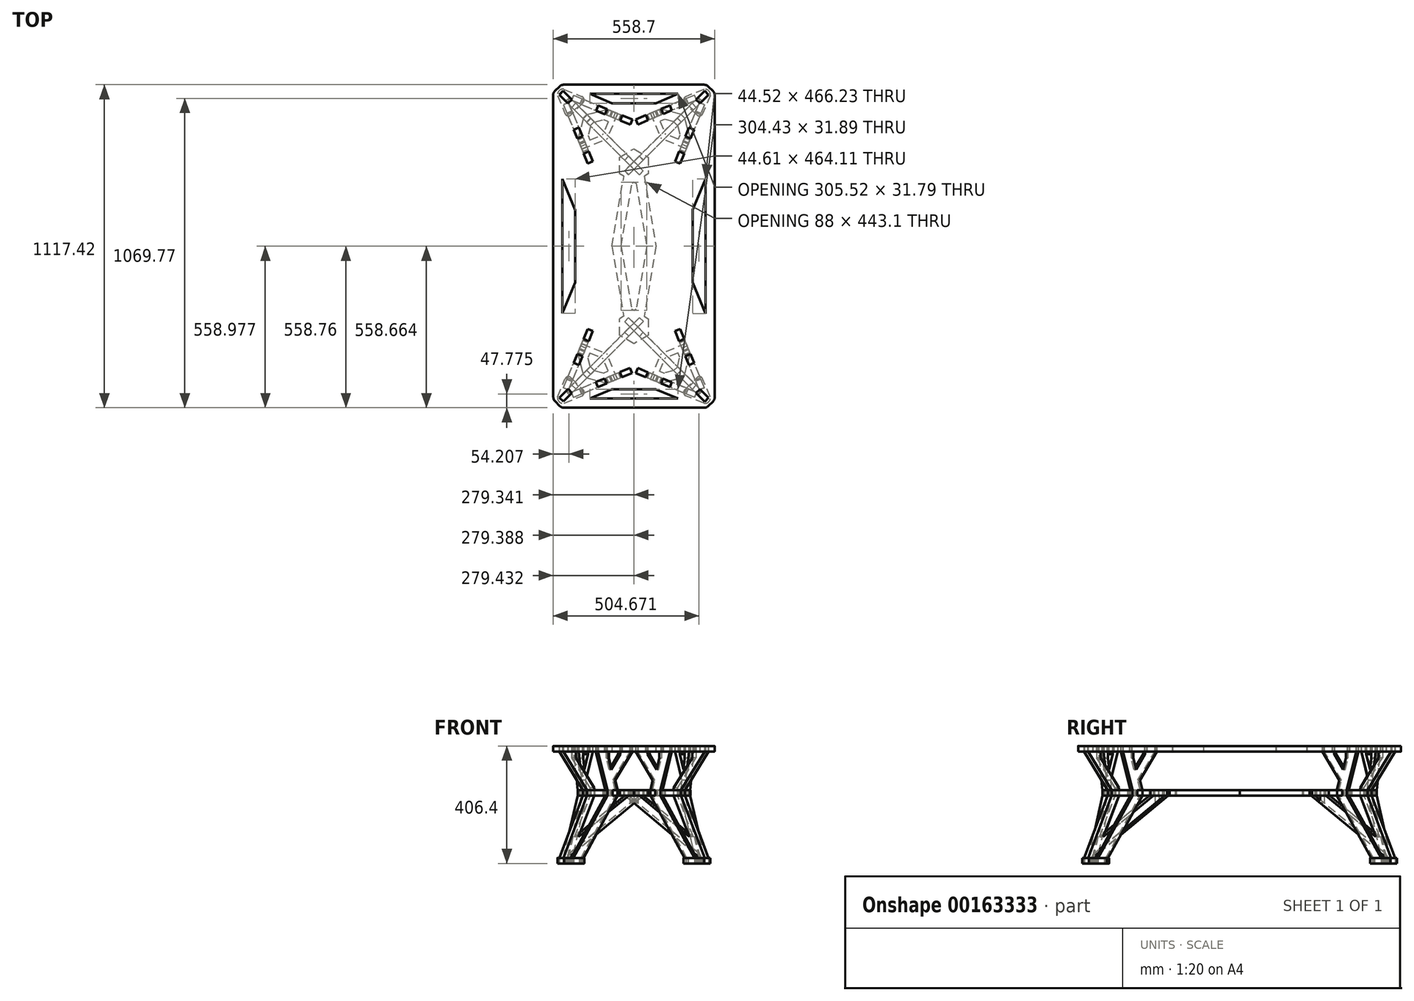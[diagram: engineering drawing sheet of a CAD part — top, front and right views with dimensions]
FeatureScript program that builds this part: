
annotation { "Feature Type Name" : "Feature", "Feature Type Description" : "" }
export const myFeature = defineFeature(function(context is Context, id is Id, definition is map)
    precondition{}
    {
        {
            var Q0;
            Q0=qCreatedBy(makeId("Top.planeOp"),FACE);
            var sketch = newSketch(context, id + "F0", { "sketchPlane" : qUnion([Q0])});
            skLineSegment(sketch, "E0.bottom", {"start": v(0.12, 1117.48) * mm, "end": v(558.92, 1117.48) * mm});
            skLineSegment(sketch, "E0.top", {"start": v(0.12, -0.12) * mm, "end": v(558.92, -0.12) * mm});
            skLineSegment(sketch, "E0.left", {"start": v(0.12, 1117.48) * mm, "end": v(0.12, -0.12) * mm});
            skLineSegment(sketch, "E0.right", {"start": v(558.92, 1117.48) * mm, "end": v(558.92, -0.12) * mm});
            skLineSegment(sketch, "E1", {"start": v(0.12, -0.12) * mm, "end": v(425.24, 425) * mm, "construction": true});
            skLineSegment(sketch, "E2", {"start": v(558.92, 1117.48) * mm, "end": v(139.82, 698.5) * mm, "construction": true});
            skLineSegment(sketch, "E3", {"start": v(0.12, 1117.48) * mm, "end": v(139.82, 1117.48) * mm});
            skLineSegment(sketch, "E4", {"start": v(139.82, 1117.48) * mm, "end": v(139.82, -0.12) * mm, "construction": true});
            skLineSegment(sketch, "E5", {"start": v(558.92, -0.12) * mm, "end": v(419.22, -0.12) * mm});
            skPoint(sketch, "E6", {"position": v(419.22, 1117.48) * mm});
            skLineSegment(sketch, "E7", {"start": v(419.22, 1117.48) * mm, "end": v(427.8, -0.12) * mm, "construction": true});
            skLineSegment(sketch, "E8.MirrorCS", {"start": v(422.46, 695.18) * mm, "end": v(0.12, 1117.48) * mm, "construction": true});
            skPoint(sketch, "E9", {"position": v(117.33, 48.6) * mm});
            skPoint(sketch, "E10", {"position": v(48.57, 117.26) * mm});
            skLineSegment(sketch, "E11", {"start": v(60.73, 105.12) * mm, "end": v(105.17, 60.75) * mm});
            skLineSegment(sketch, "E12.0", {"start": v(5.87, -2.43) * mm, "end": v(54.47, 114.9) * mm, "construction": true});
            skLineSegment(sketch, "E13.0", {"start": v(-2.43, 5.87) * mm, "end": v(114.9, 54.47) * mm, "construction": true});
            skLineSegment(sketch, "E14", {"start": v(21.87, 35.21) * mm, "end": v(44.32, 57.67) * mm});
            skLineSegment(sketch, "E15", {"start": v(35.34, 21.74) * mm, "end": v(57.8, 44.2) * mm});
            skLineSegment(sketch, "E16", {"start": v(44.32, 57.67) * mm, "end": v(57.8, 44.2) * mm});
            skLineSegment(sketch, "E17", {"start": v(21.87, 35.21) * mm, "end": v(35.34, 21.74) * mm});
            skLineSegment(sketch, "E18.0", {"start": v(44.06, 112.79) * mm, "end": v(112.85, 44.1) * mm, "construction": true});
            skLineSegment(sketch, "E19", {"start": v(47.74, 98.66) * mm, "end": v(65.34, 91.37) * mm});
            skLineSegment(sketch, "E20", {"start": v(65.34, 91.37) * mm, "end": v(53.2, 62.04) * mm});
            skLineSegment(sketch, "E21", {"start": v(53.2, 62.04) * mm, "end": v(35.6, 69.33) * mm});
            skLineSegment(sketch, "E22", {"start": v(35.6, 69.33) * mm, "end": v(47.74, 98.66) * mm});
            skLineSegment(sketch, "E23", {"start": v(98.94, 47.85) * mm, "end": v(91.65, 65.45) * mm});
            skLineSegment(sketch, "E24", {"start": v(91.65, 65.45) * mm, "end": v(62.3, 53.3) * mm});
            skLineSegment(sketch, "E25", {"start": v(62.3, 53.3) * mm, "end": v(69.6, 35.7) * mm});
            skLineSegment(sketch, "E26", {"start": v(69.6, 35.7) * mm, "end": v(98.94, 47.85) * mm});
            skPoint(sketch, "E27", {"position": v(65.95, 44.5) * mm});
            skLineSegment(sketch, "E28", {"start": v(95.3, 56.65) * mm, "end": v(426.3, 193.77) * mm, "construction": true});
            skPoint(sketch, "E29", {"position": v(44.4, 65.69) * mm});
            skLineSegment(sketch, "E30", {"start": v(44.4, 65.69) * mm, "end": v(139.82, 296.06) * mm, "construction": true});
            skPoint(sketch, "E31.orphan", {"position": v(56.54, 95.02) * mm});
            skLineSegment(sketch, "E32", {"start": v(558.92, -0.12) * mm, "end": v(530.98, 27.81) * mm, "construction": true});
            skLineSegment(sketch, "E33", {"start": v(558.92, -0.12) * mm, "end": v(555.48, 8.18) * mm});
            skLineSegment(sketch, "E34", {"start": v(558.92, -0.12) * mm, "end": v(550.62, 3.32) * mm});
            skLineSegment(sketch, "E35", {"start": v(441.55, 48.52) * mm, "end": v(446.41, 53.37) * mm});
            skLineSegment(sketch, "E36.0", {"start": v(446.04, 44.02) * mm, "end": v(514.81, 112.71) * mm, "construction": true});
            skLineSegment(sketch, "E37.0", {"start": v(553.05, -2.56) * mm, "end": v(504.46, 114.77) * mm, "construction": true});
            skLineSegment(sketch, "E38.0", {"start": v(561.3, 5.76) * mm, "end": v(443.98, 54.38) * mm, "construction": true});
            skLineSegment(sketch, "E39", {"start": v(524.24, 21.07) * mm, "end": v(501.79, 43.52) * mm});
            skLineSegment(sketch, "E40", {"start": v(501.79, 43.52) * mm, "end": v(515.26, 57) * mm});
            skLineSegment(sketch, "E41", {"start": v(515.26, 57) * mm, "end": v(537.7, 34.54) * mm});
            skLineSegment(sketch, "E42", {"start": v(524.24, 21.07) * mm, "end": v(537.7, 34.54) * mm});
            skLineSegment(sketch, "E43", {"start": v(460.07, 47.71) * mm, "end": v(467.3, 65.18) * mm});
            skLineSegment(sketch, "E44", {"start": v(467.3, 65.18) * mm, "end": v(496.64, 53.02) * mm});
            skLineSegment(sketch, "E45", {"start": v(496.64, 53.02) * mm, "end": v(489.4, 35.56) * mm});
            skLineSegment(sketch, "E46", {"start": v(489.4, 35.56) * mm, "end": v(460.07, 47.71) * mm});
            skLineSegment(sketch, "E47", {"start": v(511.05, 98.85) * mm, "end": v(493.45, 91.56) * mm});
            skLineSegment(sketch, "E48", {"start": v(493.45, 91.56) * mm, "end": v(505.6, 62.23) * mm});
            skLineSegment(sketch, "E49", {"start": v(505.6, 62.23) * mm, "end": v(523.2, 69.52) * mm});
            skLineSegment(sketch, "E50", {"start": v(523.2, 69.52) * mm, "end": v(511.05, 98.85) * mm});
            skPoint(sketch, "E51", {"position": v(493.02, 44.29) * mm});
            skPoint(sketch, "E52", {"position": v(514.4, 65.87) * mm});
            skLineSegment(sketch, "E53", {"start": v(514.4, 65.87) * mm, "end": v(425.64, 280.16) * mm, "construction": true});
            skLineSegment(sketch, "E54", {"start": v(493.02, 44.29) * mm, "end": v(139.82, 190.66) * mm, "construction": true});
            skPoint(sketch, "E55.first.point", {"position": v(7.35, 17.5) * mm});
            skPoint(sketch, "E55.second.point", {"position": v(17.7, 7.2) * mm});
            skArc(sketch, "E56", {"start": v(7.35, 17.5) * mm, "mid": v(9.84, 9.66) * mm, "end": v(17.7, 7.2) * mm, "construction": true});
            skPoint(sketch, "E57", {"position": v(103.85, 62.06) * mm});
            skPoint(sketch, "E58", {"position": v(99.73, 41.31) * mm});
            skArc(sketch, "E59", {"start": v(99.73, 41.31) * mm, "mid": v(107.37, 50.58) * mm, "end": v(103.85, 62.06) * mm});
            skPoint(sketch, "E60", {"position": v(41.28, 99.66) * mm});
            skPoint(sketch, "E61", {"position": v(62.05, 103.8) * mm});
            skArc(sketch, "E62", {"start": v(62.05, 103.8) * mm, "mid": v(50.55, 107.31) * mm, "end": v(41.28, 99.66) * mm});
            skLineSegment(sketch, "E63.trimOffspring", {"start": v(15.71, 37.76) * mm, "end": v(41.33, 99.8) * mm});
            skLineSegment(sketch, "E64.trimOffspring", {"start": v(37.9, 15.6) * mm, "end": v(99.85, 41.36) * mm});
            skLineSegment(sketch, "E65", {"start": v(35.34, 21.74) * mm, "end": v(37.9, 15.6) * mm, "construction": true});
            skLineSegment(sketch, "E66", {"start": v(21.87, 35.21) * mm, "end": v(15.71, 37.76) * mm, "construction": true});
            skArc(sketch, "E67", {"start": v(15.71, 37.76) * mm, "mid": v(21, 20.86) * mm, "end": v(37.9, 15.6) * mm});
            skPoint(sketch, "E68", {"position": v(459.15, 41.22) * mm});
            skPoint(sketch, "E69", {"position": v(517.74, 99.3) * mm});
            skPoint(sketch, "E70", {"position": v(455.03, 61.98) * mm});
            skPoint(sketch, "E71", {"position": v(496.84, 103.74) * mm});
            skLineSegment(sketch, "E72", {"start": v(524.24, 21.07) * mm, "end": v(521.82, 15.25) * mm, "construction": true});
            skLineSegment(sketch, "E73", {"start": v(537.7, 34.54) * mm, "end": v(543.56, 36.96) * mm, "construction": true});
            skArc(sketch, "E74", {"start": v(455.03, 61.98) * mm, "mid": v(451.52, 50.5) * mm, "end": v(459.15, 41.22) * mm});
            skArc(sketch, "E75", {"start": v(517.74, 99.3) * mm, "mid": v(508.5, 107.22) * mm, "end": v(496.84, 103.74) * mm});
            skArc(sketch, "E76", {"start": v(521.82, 15.25) * mm, "mid": v(538.2, 20.6) * mm, "end": v(543.56, 36.96) * mm});
            skLineSegment(sketch, "E77.trimOffspring", {"start": v(521.82, 15.25) * mm, "end": v(459.08, 41.25) * mm});
            skLineSegment(sketch, "E78.trimOffspring", {"start": v(543.56, 36.96) * mm, "end": v(517.44, 100.01) * mm});
            skLineSegment(sketch, "E79.trimOffspring", {"start": v(512.95, 110.85) * mm, "end": v(510.32, 117.2) * mm});
            skLineSegment(sketch, "E80.trimOffspring", {"start": v(505.46, 112.35) * mm, "end": v(510.32, 117.2) * mm});
            skLineSegment(sketch, "E81.trimOffspring", {"start": v(453.65, 60.6) * mm, "end": v(498.17, 105.06) * mm});
            skLineSegment(sketch, "E82.trimOffspring", {"start": v(447.9, 45.88) * mm, "end": v(441.55, 48.52) * mm});
            skLineSegment(sketch, "E83", {"start": v(37.26, 1102.12) * mm, "end": v(99.78, 1076.27) * mm});
            skLineSegment(sketch, "E84", {"start": v(15.48, 1080.34) * mm, "end": v(41.33, 1017.86) * mm});
            skLineSegment(sketch, "E85", {"start": v(103.9, 1055.58) * mm, "end": v(62.08, 1013.73) * mm});
            skLineSegment(sketch, "E86.0", {"start": v(11.84, 1105.76) * mm, "end": v(106.12, 1066.78) * mm, "construction": true});
            skLineSegment(sketch, "E86.1", {"start": v(11.84, 1105.76) * mm, "end": v(50.84, 1011.47) * mm, "construction": true});
            skLineSegment(sketch, "E86.2", {"start": v(106.12, 1066.78) * mm, "end": v(50.84, 1011.47) * mm, "construction": true});
            skLineSegment(sketch, "E87", {"start": v(21.37, 1082.78) * mm, "end": v(43.83, 1060.33) * mm});
            skLineSegment(sketch, "E88", {"start": v(34.84, 1096.25) * mm, "end": v(57.29, 1073.8) * mm});
            skLineSegment(sketch, "E89", {"start": v(43.83, 1060.33) * mm, "end": v(57.29, 1073.8) * mm});
            skLineSegment(sketch, "E90", {"start": v(21.37, 1082.78) * mm, "end": v(34.84, 1096.25) * mm});
            skLineSegment(sketch, "E91", {"start": v(47.82, 1018.79) * mm, "end": v(65.42, 1026.07) * mm});
            skLineSegment(sketch, "E92", {"start": v(65.42, 1026.07) * mm, "end": v(53.28, 1055.4) * mm});
            skLineSegment(sketch, "E93", {"start": v(53.28, 1055.4) * mm, "end": v(35.68, 1048.13) * mm});
            skLineSegment(sketch, "E94", {"start": v(35.68, 1048.13) * mm, "end": v(47.82, 1018.79) * mm});
            skLineSegment(sketch, "E95", {"start": v(100.12, 1069.26) * mm, "end": v(92.84, 1051.65) * mm});
            skLineSegment(sketch, "E96", {"start": v(92.84, 1051.65) * mm, "end": v(63.5, 1063.78) * mm});
            skLineSegment(sketch, "E97", {"start": v(63.5, 1063.78) * mm, "end": v(70.78, 1081.39) * mm});
            skLineSegment(sketch, "E98", {"start": v(70.78, 1081.39) * mm, "end": v(100.12, 1069.26) * mm});
            skPoint(sketch, "E99", {"position": v(99.73, 1076.3) * mm});
            skPoint(sketch, "E100", {"position": v(103.87, 1055.54) * mm});
            skPoint(sketch, "E101", {"position": v(62.08, 1013.73) * mm});
            skPoint(sketch, "E102", {"position": v(41.33, 1017.86) * mm});
            skLineSegment(sketch, "E103", {"start": v(34.84, 1096.25) * mm, "end": v(37.26, 1102.12) * mm, "construction": true});
            skLineSegment(sketch, "E104", {"start": v(21.37, 1082.78) * mm, "end": v(15.48, 1080.34) * mm, "construction": true});
            skArc(sketch, "E105", {"start": v(37.26, 1102.12) * mm, "mid": v(20.83, 1096.78) * mm, "end": v(15.48, 1080.34) * mm});
            skArc(sketch, "E106", {"start": v(41.33, 1017.86) * mm, "mid": v(50.6, 1010.25) * mm, "end": v(62.08, 1013.73) * mm});
            skArc(sketch, "E107", {"start": v(103.87, 1055.54) * mm, "mid": v(107.36, 1067.02) * mm, "end": v(99.73, 1076.3) * mm});
            skPoint(sketch, "E108.orphan", {"position": v(117.33, 1069.01) * mm});
            skPoint(sketch, "E109.orphan", {"position": v(48.61, 1000.26) * mm});
            skPoint(sketch, "E110", {"position": v(67.14, 1072.59) * mm});
            skPoint(sketch, "E111", {"position": v(44.48, 1051.77) * mm});
            skLineSegment(sketch, "E112", {"start": v(67.14, 1072.59) * mm, "end": v(420.68, 926.4) * mm, "construction": true});
            skLineSegment(sketch, "E113", {"start": v(44.48, 1051.77) * mm, "end": v(139.82, 821.33) * mm, "construction": true});
            skLineSegment(sketch, "E114", {"start": v(543.54, 1080.37) * mm, "end": v(517.57, 1017.7) * mm});
            skLineSegment(sketch, "E115", {"start": v(521.77, 1102.1) * mm, "end": v(459, 1076.1) * mm});
            skLineSegment(sketch, "E116", {"start": v(496.86, 1013.59) * mm, "end": v(454.91, 1055.55) * mm});
            skLineSegment(sketch, "E117.0", {"start": v(547.18, 1105.75) * mm, "end": v(508.07, 1011.36) * mm, "construction": true});
            skLineSegment(sketch, "E117.1", {"start": v(547.18, 1105.75) * mm, "end": v(452.79, 1066.66) * mm, "construction": true});
            skLineSegment(sketch, "E117.2", {"start": v(508.07, 1011.36) * mm, "end": v(452.79, 1066.66) * mm, "construction": true});
            skLineSegment(sketch, "E118", {"start": v(524.18, 1096.28) * mm, "end": v(501.73, 1073.84) * mm});
            skLineSegment(sketch, "E119", {"start": v(501.73, 1073.84) * mm, "end": v(515.2, 1060.36) * mm});
            skLineSegment(sketch, "E120", {"start": v(515.2, 1060.36) * mm, "end": v(537.65, 1082.81) * mm});
            skLineSegment(sketch, "E121", {"start": v(537.65, 1082.81) * mm, "end": v(524.18, 1096.28) * mm});
            skLineSegment(sketch, "E122", {"start": v(511.1, 1018.66) * mm, "end": v(493.5, 1025.96) * mm});
            skLineSegment(sketch, "E123", {"start": v(493.5, 1025.96) * mm, "end": v(505.65, 1055.29) * mm});
            skLineSegment(sketch, "E124", {"start": v(505.65, 1055.29) * mm, "end": v(523.25, 1048) * mm});
            skLineSegment(sketch, "E125", {"start": v(523.25, 1048) * mm, "end": v(511.1, 1018.66) * mm});
            skLineSegment(sketch, "E126", {"start": v(460.07, 1069.68) * mm, "end": v(467.36, 1052.07) * mm});
            skLineSegment(sketch, "E127", {"start": v(467.36, 1052.07) * mm, "end": v(496.7, 1064.22) * mm});
            skLineSegment(sketch, "E128", {"start": v(496.7, 1064.22) * mm, "end": v(489.4, 1081.82) * mm});
            skLineSegment(sketch, "E129", {"start": v(489.4, 1081.82) * mm, "end": v(460.07, 1069.68) * mm});
            skPoint(sketch, "E130", {"position": v(517.6, 1017.75) * mm});
            skPoint(sketch, "E131", {"position": v(496.83, 1013.62) * mm});
            skPoint(sketch, "E132", {"position": v(455.05, 1055.42) * mm});
            skPoint(sketch, "E133", {"position": v(459.18, 1076.18) * mm});
            skLineSegment(sketch, "E134", {"start": v(524.18, 1096.28) * mm, "end": v(521.77, 1102.1) * mm, "construction": true});
            skLineSegment(sketch, "E135", {"start": v(537.65, 1082.81) * mm, "end": v(543.54, 1080.37) * mm, "construction": true});
            skArc(sketch, "E136", {"start": v(543.54, 1080.37) * mm, "mid": v(538.16, 1096.75) * mm, "end": v(521.77, 1102.1) * mm});
            skArc(sketch, "E137", {"start": v(459.18, 1076.18) * mm, "mid": v(451.52, 1066.91) * mm, "end": v(455.05, 1055.42) * mm});
            skArc(sketch, "E138", {"start": v(496.83, 1013.62) * mm, "mid": v(508.32, 1010.13) * mm, "end": v(517.6, 1017.75) * mm});
            skPoint(sketch, "E139.orphan", {"position": v(510.3, 1000.15) * mm});
            skPoint(sketch, "E140.orphan", {"position": v(441.58, 1068.89) * mm});
            skPoint(sketch, "E141", {"position": v(514.45, 1051.64) * mm});
            skPoint(sketch, "E142", {"position": v(493.05, 1073.02) * mm});
            skLineSegment(sketch, "E143", {"start": v(514.45, 1051.64) * mm, "end": v(421.45, 827.2) * mm, "construction": true});
            skLineSegment(sketch, "E144", {"start": v(493.05, 1073.02) * mm, "end": v(139.82, 926.75) * mm, "construction": true});
            skLineSegment(sketch, "E145.trimOffspring", {"start": v(508.53, 50.26) * mm, "end": v(139.82, 418.98) * mm, "construction": true});
            skSolve(sketch);
        }
        {
            var Q0;
            Q0=sQuery(id+"F0.wireOp",EDGE,"E1");
            var Q1;
            {var subQ1=sQuery(id+"F0.wireOp",EDGE,"E1");var subQ7=sQuery(id+"F0.wireOp",EDGE,"E4");var subQ9=makeQuery(id+"F0.imprint","INTERSECT",VERTEX,{"derivedFrom":[subQ1,subQ7]});Q1=makeQuery(id+"F0.imprint","IMPRINT",FACE,{"disambiguationData":[TD([[makeQuery(id+"F0.imprint","IMPRINT",EDGE,{"disambiguationData":[TD([[subQ9,-1.0]])],"derivedFrom":subQ1}),-1.0]])]});}
            cPlane(context, id + "F1", {"entities" : qUnion([Q0, Q1]), "cplaneType" : CPlaneType.LINE_ANGLE, "offset" : 25.4 * mm, "angle" : 90 * degree, "width" : 152.4 * mm, "height" : 152.4 * mm});
        }
        {
            var Q0;
            Q0=qCreatedBy(id+"F1.planeOp",FACE);
            var sketch = newSketch(context, id + "F2", { "sketchPlane" : qUnion([Q0])});
            skLineSegment(sketch, "E146", {"start": v(603.86, 0) * mm, "end": v(603.86, 406.4) * mm, "construction": true});
            skLineSegment(sketch, "E147.MirrorCS", {"start": v(72.14, 19.05) * mm, "end": v(76.5, 19.05) * mm});
            skLineSegment(sketch, "E148.MirrorCS", {"start": v(40.4, 387.35) * mm, "end": v(40.4, 406.4) * mm});
            skLineSegment(sketch, "E149.MirrorCS", {"start": v(40.4, 19.05) * mm, "end": v(40.4, 0) * mm});
            skLineSegment(sketch, "E150.MirrorCS", {"start": v(82.38, 406.4) * mm, "end": v(40.4, 406.4) * mm});
            skLineSegment(sketch, "E151.MirrorCS", {"start": v(40.4, 387.35) * mm, "end": v(603.86, 387.35) * mm, "construction": true});
            skLineSegment(sketch, "E152.MirrorCS", {"start": v(40.4, 406.4) * mm, "end": v(603.86, 406.4) * mm, "construction": true});
            skLineSegment(sketch, "E153.MirrorCS", {"start": v(40.4, 0) * mm, "end": v(40.4, 406.4) * mm, "construction": true});
            skPoint(sketch, "E154.MirrorP", {"position": v(40.4, 254) * mm});
            skLineSegment(sketch, "E155.MirrorCS", {"start": v(82.38, 387.35) * mm, "end": v(82.38, 406.4) * mm});
            skLineSegment(sketch, "E156.MirrorCS", {"start": v(40.4, 0) * mm, "end": v(72.14, 0) * mm});
            skLineSegment(sketch, "E157.MirrorCS", {"start": v(155.77, 254) * mm, "end": v(40.4, 387.35) * mm});
            skLineSegment(sketch, "E158.MirrorCS", {"start": v(72.14, 19.05) * mm, "end": v(72.14, 0) * mm});
            skLineSegment(sketch, "E159.MirrorCS", {"start": v(40.4, 19.05) * mm, "end": v(155.77, 234.95) * mm});
            skLineSegment(sketch, "E160.MirrorCS", {"start": v(76.5, 19.05) * mm, "end": v(603.86, 19.05) * mm, "construction": true});
            skLineSegment(sketch, "E161.MirrorCS", {"start": v(72.14, 0) * mm, "end": v(603.86, 0) * mm, "construction": true});
            skLineSegment(sketch, "E162.trimOffspring", {"start": v(115.25, 91.77) * mm, "end": v(191.77, 234.95) * mm});
            skLineSegment(sketch, "E163", {"start": v(82.67, 30.78) * mm, "end": v(76.5, 19.05) * mm});
            skLineSegment(sketch, "E164", {"start": v(40.4, 254) * mm, "end": v(155.77, 254) * mm, "construction": true});
            skLineSegment(sketch, "E165.0", {"start": v(40.4, 234.95) * mm, "end": v(191.77, 234.95) * mm, "construction": true});
            skLineSegment(sketch, "E166", {"start": v(82.67, 30.78) * mm, "end": v(431.82, 234.95) * mm});
            skLineSegment(sketch, "E167", {"start": v(191.77, 234.95) * mm, "end": v(191.77, 260.91) * mm});
            skLineSegment(sketch, "E168.trimOffspring", {"start": v(191.77, 260.91) * mm, "end": v(101.43, 365.33) * mm});
            skLineSegment(sketch, "E169.trimOffspring", {"start": v(173.77, 254) * mm, "end": v(360.6, 254) * mm, "construction": true});
            skLineSegment(sketch, "E170.trimOffspring", {"start": v(191.77, 234.95) * mm, "end": v(603.86, 234.95) * mm, "construction": true});
            skLineSegment(sketch, "E171", {"start": v(155.77, 254) * mm, "end": v(173.77, 254) * mm});
            skLineSegment(sketch, "E172", {"start": v(173.77, 254) * mm, "end": v(173.77, 234.95) * mm});
            skLineSegment(sketch, "E173", {"start": v(173.77, 234.95) * mm, "end": v(155.77, 234.95) * mm});
            skLineSegment(sketch, "E174", {"start": v(395.13, 0) * mm, "end": v(395.13, 406.4) * mm, "construction": true});
            skLineSegment(sketch, "E175", {"start": v(431.82, 234.95) * mm, "end": v(431.82, 254) * mm});
            skLineSegment(sketch, "E176", {"start": v(385.6, 207.92) * mm, "end": v(385.6, 254) * mm, "construction": true});
            skLineSegment(sketch, "E177", {"start": v(404.65, 219.06) * mm, "end": v(404.65, 254) * mm, "construction": true});
            skLineSegment(sketch, "E178.trimOffspring", {"start": v(431.82, 254) * mm, "end": v(603.86, 254) * mm, "construction": true});
            skLineSegment(sketch, "E179", {"start": v(360.12, 254) * mm, "end": v(385.6, 254) * mm});
            skLineSegment(sketch, "E180.0", {"start": v(115.25, 91.77) * mm, "end": v(360.12, 234.95) * mm});
            skLineSegment(sketch, "E181", {"start": v(360.12, 234.95) * mm, "end": v(360.12, 254) * mm});
            skLineSegment(sketch, "E182", {"start": v(404.65, 254) * mm, "end": v(404.65, 234.95) * mm});
            skLineSegment(sketch, "E183", {"start": v(404.65, 234.95) * mm, "end": v(385.6, 234.95) * mm});
            skLineSegment(sketch, "E184", {"start": v(385.6, 234.95) * mm, "end": v(385.6, 254) * mm});
            skLineSegment(sketch, "E185.trimOffspring", {"start": v(404.65, 254) * mm, "end": v(431.82, 254) * mm});
            skLineSegment(sketch, "E186", {"start": v(82.38, 387.35) * mm, "end": v(101.43, 387.35) * mm});
            skLineSegment(sketch, "E187", {"start": v(101.43, 365.33) * mm, "end": v(101.43, 387.35) * mm});
            skSolve(sketch);
        }
        {
            var Q0;
            Q0=makeQuery(id+"F2.imprint","IMPRINT",FACE,{"disambiguationData":[TD([[makeQuery(id+"F2.imprint","IMPRINT",EDGE,{"derivedFrom":sQuery(id+"F2.wireOp",EDGE,"E147.MirrorCS")}),1.0]])]});
            extrude(context, id + "F3", {"entities" : qUnion([Q0]), "endBound" : BoundingType.SYMMETRIC, "depth" : 19.05 * mm});
        }
        {
            var Q0;
            Q0=sQuery(id+"F0.wireOp",EDGE,"E28");
            cPlane(context, id + "F4", {"entities" : qUnion([Q0]), "cplaneType" : CPlaneType.LINE_ANGLE, "offset" : 25.4 * mm, "angle" : 0 * degree, "width" : 152.4 * mm, "height" : 152.4 * mm});
        }
        {
            var Q0;
            Q0=qCreatedBy(id+"F4.planeOp",FACE);
            var sketch = newSketch(context, id + "F5", { "sketchPlane" : qUnion([Q0])});
            skLineSegment(sketch, "E188", {"start": v(-442.84, 0) * mm, "end": v(-442.84, 406.4) * mm, "construction": true});
            skLineSegment(sketch, "E189.MirrorCS", {"start": v(-109.72, 19.05) * mm, "end": v(-114.91, 19.05) * mm});
            skLineSegment(sketch, "E190.MirrorCS", {"start": v(-77.97, 19.05) * mm, "end": v(-77.97, 0) * mm});
            skLineSegment(sketch, "E191.MirrorCS", {"start": v(-109.72, 0) * mm, "end": v(-109.72, 19.05) * mm});
            skLineSegment(sketch, "E192.MirrorCS", {"start": v(-77.97, 0) * mm, "end": v(-109.72, 0) * mm});
            skLineSegment(sketch, "E193.MirrorCS", {"start": v(-77.97, 234.95) * mm, "end": v(-206.36, 234.95) * mm, "construction": true});
            skLineSegment(sketch, "E194.MirrorCS", {"start": v(-77.97, 387.35) * mm, "end": v(-442.84, 387.35) * mm, "construction": true});
            skLineSegment(sketch, "E195.MirrorCS", {"start": v(-77.97, 0) * mm, "end": v(-442.84, 0) * mm, "construction": true});
            skLineSegment(sketch, "E196.MirrorCS", {"start": v(-77.97, 406.4) * mm, "end": v(-442.84, 406.4) * mm, "construction": true});
            skLineSegment(sketch, "E197.MirrorCS", {"start": v(-77.97, 0) * mm, "end": v(-77.97, 406.4) * mm, "construction": true});
            skLineSegment(sketch, "E198.MirrorCS", {"start": v(-309, 0) * mm, "end": v(-309, 406.4) * mm, "construction": true});
            skLineSegment(sketch, "E199", {"start": v(-77.97, 19.05) * mm, "end": v(-206.36, 234.95) * mm});
            skLineSegment(sketch, "E200", {"start": v(-206.36, 234.95) * mm, "end": v(-206.36, 254) * mm});
            skLineSegment(sketch, "E201", {"start": v(-206.36, 254) * mm, "end": v(-170.87, 387.35) * mm});
            skLineSegment(sketch, "E202", {"start": v(-170.87, 387.35) * mm, "end": v(-170.87, 406.4) * mm});
            skLineSegment(sketch, "E203", {"start": v(-220.38, 324.76) * mm, "end": v(-254.06, 377.42) * mm});
            skLineSegment(sketch, "E204.0", {"start": v(-234.34, 287.65) * mm, "end": v(-298.1, 387.35) * mm});
            skLineSegment(sketch, "E205", {"start": v(-224.83, 234.95) * mm, "end": v(-243.3, 234.95) * mm});
            skPoint(sketch, "E206", {"position": v(-224.83, 234.95) * mm});
            skLineSegment(sketch, "E207", {"start": v(-224.83, 234.95) * mm, "end": v(-224.83, 254) * mm});
            skLineSegment(sketch, "E208.trimOffspring", {"start": v(-309, 254) * mm, "end": v(-442.84, 254) * mm, "construction": true});
            skLineSegment(sketch, "E209", {"start": v(-243.3, 254) * mm, "end": v(-224.83, 254) * mm});
            skLineSegment(sketch, "E210.trimOffspring", {"start": v(-224.83, 234.95) * mm, "end": v(-442.84, 234.95) * mm, "construction": true});
            skLineSegment(sketch, "E211.trimOffspring", {"start": v(-220.38, 324.76) * mm, "end": v(-210.07, 363.49) * mm});
            skLineSegment(sketch, "E212", {"start": v(-203.72, 387.35) * mm, "end": v(-203.72, 406.4) * mm});
            skLineSegment(sketch, "E213", {"start": v(-203.72, 406.4) * mm, "end": v(-170.87, 406.4) * mm});
            skLineSegment(sketch, "E214", {"start": v(-260.4, 387.35) * mm, "end": v(-260.4, 406.4) * mm});
            skLineSegment(sketch, "E215", {"start": v(-298.1, 387.35) * mm, "end": v(-298.1, 406.4) * mm});
            skLineSegment(sketch, "E216", {"start": v(-298.1, 406.4) * mm, "end": v(-260.4, 406.4) * mm});
            skLineSegment(sketch, "E217.trimOffspring", {"start": v(-114.91, 19.05) * mm, "end": v(-243.3, 234.95) * mm});
            skLineSegment(sketch, "E218", {"start": v(-243.3, 254) * mm, "end": v(-234.34, 287.65) * mm});
            skPoint(sketch, "E219", {"position": v(-210.07, 387.35) * mm});
            skPoint(sketch, "E220", {"position": v(-254.06, 387.35) * mm});
            skLineSegment(sketch, "E221", {"start": v(-203.72, 387.35) * mm, "end": v(-210.07, 387.35) * mm});
            skLineSegment(sketch, "E222", {"start": v(-210.07, 363.49) * mm, "end": v(-210.07, 387.35) * mm});
            skLineSegment(sketch, "E223", {"start": v(-254.06, 387.35) * mm, "end": v(-260.4, 387.35) * mm});
            skLineSegment(sketch, "E224", {"start": v(-254.06, 387.35) * mm, "end": v(-254.06, 377.42) * mm});
            skSolve(sketch);
        }
        {
            var Q0;
            Q0=makeQuery(id+"F5.imprint","IMPRINT",FACE,{"disambiguationData":[TD([[makeQuery(id+"F5.imprint","IMPRINT",EDGE,{"derivedFrom":sQuery(id+"F5.wireOp",EDGE,"E189.MirrorCS")}),-1.0]])]});
            extrude(context, id + "F6", {"entities" : qUnion([Q0]), "endBound" : BoundingType.SYMMETRIC, "depth" : 19.05 * mm});
        }
        {
            var Q0;
            Q0=sQuery(id+"F0.wireOp",EDGE,"E30");
            cPlane(context, id + "F7", {"entities" : qUnion([Q0]), "cplaneType" : CPlaneType.LINE_ANGLE, "offset" : 25.4 * mm, "angle" : 90 * degree, "width" : 152.4 * mm, "height" : 152.4 * mm});
        }
        {
            var Q0;
            Q0=qCreatedBy(id+"F7.planeOp",FACE);
            var sketch = newSketch(context, id + "F8", { "sketchPlane" : qUnion([Q0])});
            skLineSegment(sketch, "E225", {"start": v(442.55, 0) * mm, "end": v(442.55, 406.4) * mm, "construction": true});
            skLineSegment(sketch, "E226.MirrorCS", {"start": v(206.06, 234.95) * mm, "end": v(206.06, 254) * mm});
            skLineSegment(sketch, "E227.MirrorCS", {"start": v(203.42, 406.4) * mm, "end": v(170.57, 406.4) * mm});
            skLineSegment(sketch, "E228.MirrorCS", {"start": v(77.67, 19.05) * mm, "end": v(77.67, 0) * mm});
            skLineSegment(sketch, "E229.MirrorCS", {"start": v(109.42, 19.05) * mm, "end": v(114.61, 19.05) * mm});
            skLineSegment(sketch, "E230.MirrorCS", {"start": v(224.53, 234.95) * mm, "end": v(243, 234.95) * mm});
            skLineSegment(sketch, "E231.MirrorCS", {"start": v(297.8, 406.4) * mm, "end": v(260.1, 406.4) * mm});
            skLineSegment(sketch, "E232.MirrorCS", {"start": v(77.67, 0) * mm, "end": v(109.42, 0) * mm});
            skLineSegment(sketch, "E233.MirrorCS", {"start": v(260.1, 387.35) * mm, "end": v(260.1, 406.4) * mm});
            skLineSegment(sketch, "E234.MirrorCS", {"start": v(109.42, 0) * mm, "end": v(109.42, 19.05) * mm});
            skLineSegment(sketch, "E235.MirrorCS", {"start": v(77.67, 406.4) * mm, "end": v(442.55, 406.4) * mm, "construction": true});
            skLineSegment(sketch, "E236.MirrorCS", {"start": v(220.08, 324.76) * mm, "end": v(209.77, 363.49) * mm});
            skLineSegment(sketch, "E237.MirrorCS", {"start": v(203.42, 387.35) * mm, "end": v(203.42, 406.4) * mm});
            skLineSegment(sketch, "E238.MirrorCS", {"start": v(77.67, 0) * mm, "end": v(77.67, 406.4) * mm, "construction": true});
            skLineSegment(sketch, "E239.MirrorCS", {"start": v(224.53, 234.95) * mm, "end": v(442.55, 234.95) * mm, "construction": true});
            skLineSegment(sketch, "E240.MirrorCS", {"start": v(170.57, 387.35) * mm, "end": v(170.57, 406.4) * mm});
            skLineSegment(sketch, "E241.MirrorCS", {"start": v(308.7, 254) * mm, "end": v(442.55, 254) * mm, "construction": true});
            skLineSegment(sketch, "E242.MirrorCS", {"start": v(220.08, 324.76) * mm, "end": v(253.76, 377.42) * mm});
            skLineSegment(sketch, "E243.MirrorCS", {"start": v(77.67, 387.35) * mm, "end": v(442.55, 387.35) * mm, "construction": true});
            skLineSegment(sketch, "E244.MirrorCS", {"start": v(77.67, 0) * mm, "end": v(442.55, 0) * mm, "construction": true});
            skPoint(sketch, "E245.MirrorP", {"position": v(224.53, 234.95) * mm});
            skLineSegment(sketch, "E246.MirrorCS", {"start": v(77.67, 19.05) * mm, "end": v(206.06, 234.95) * mm});
            skLineSegment(sketch, "E247.MirrorCS", {"start": v(308.7, 0) * mm, "end": v(308.7, 406.4) * mm, "construction": true});
            skLineSegment(sketch, "E248.MirrorCS", {"start": v(77.67, 254) * mm, "end": v(224.53, 254) * mm, "construction": true});
            skLineSegment(sketch, "E249.MirrorCS", {"start": v(77.67, 234.95) * mm, "end": v(206.06, 234.95) * mm, "construction": true});
            skLineSegment(sketch, "E250.MirrorCS", {"start": v(234.04, 287.65) * mm, "end": v(297.8, 387.35) * mm});
            skLineSegment(sketch, "E251.MirrorCS", {"start": v(206.06, 254) * mm, "end": v(170.57, 387.35) * mm});
            skLineSegment(sketch, "E252.MirrorCS", {"start": v(224.53, 234.95) * mm, "end": v(224.53, 254) * mm});
            skLineSegment(sketch, "E253.MirrorCS", {"start": v(297.8, 387.35) * mm, "end": v(297.8, 406.4) * mm});
            skLineSegment(sketch, "E254.MirrorCS", {"start": v(75.24, 387.35) * mm, "end": v(440.11, 387.35) * mm, "construction": true});
            skLineSegment(sketch, "E255.trimOffspring", {"start": v(114.61, 19.05) * mm, "end": v(243, 234.95) * mm});
            skLineSegment(sketch, "E256", {"start": v(243, 254) * mm, "end": v(234.04, 287.65) * mm});
            skLineSegment(sketch, "E257", {"start": v(224.53, 254) * mm, "end": v(243, 254) * mm});
            skPoint(sketch, "E258", {"position": v(253.76, 387.35) * mm});
            skPoint(sketch, "E259", {"position": v(209.77, 387.35) * mm});
            skLineSegment(sketch, "E260", {"start": v(260.1, 387.35) * mm, "end": v(253.76, 387.35) * mm});
            skLineSegment(sketch, "E261", {"start": v(253.76, 377.42) * mm, "end": v(253.76, 387.35) * mm});
            skLineSegment(sketch, "E262", {"start": v(203.42, 387.35) * mm, "end": v(209.77, 387.35) * mm});
            skLineSegment(sketch, "E263", {"start": v(209.77, 363.49) * mm, "end": v(209.77, 387.35) * mm});
            skSolve(sketch);
        }
        {
            var Q0;
            Q0=makeQuery(id+"F8.imprint","IMPRINT",FACE,{"disambiguationData":[TD([[makeQuery(id+"F8.imprint","IMPRINT",EDGE,{"derivedFrom":sQuery(id+"F8.wireOp",EDGE,"E229.MirrorCS")}),1.0]])]});
            extrude(context, id + "F9", {"entities" : qUnion([Q0]), "endBound" : BoundingType.SYMMETRIC, "depth" : 19.05 * mm});
        }
        {
            var Q0;
            Q0=makeQuery(id+"F3.opExtrude","SWEPT_FACE",FACE,{"disambiguationData":[OSD([sQuery(id+"F2.wireOp",EDGE,"E173")])]});
            cPlane(context, id + "F10", {"entities" : qUnion([Q0]), "cplaneType" : CPlaneType.OFFSET, "offset" : 0 * mm, "width" : 152.4 * mm, "height" : 152.4 * mm});
        }
        {
            var Q0;
            Q0=qCreatedBy(id+"F10.planeOp",FACE);
            var sketch = newSketch(context, id + "F11", { "sketchPlane" : qUnion([Q0])});
            skLineSegment(sketch, "E264", {"start": v(188.22, 84.84) * mm, "end": v(180.93, 102.44) * mm});
            skLineSegment(sketch, "E265", {"start": v(98.86, 222.07) * mm, "end": v(91.79, 205) * mm});
            skLineSegment(sketch, "E266", {"start": v(129.6, 116.13) * mm, "end": v(142.34, 128.86) * mm});
            skLineSegment(sketch, "E267", {"start": v(91.79, 205) * mm, "end": v(109.4, 197.72) * mm});
            skLineSegment(sketch, "E268", {"start": v(109.4, 197.72) * mm, "end": v(102.32, 180.64) * mm});
            skLineSegment(sketch, "E269", {"start": v(103.4, 116.88) * mm, "end": v(116.88, 103.4) * mm});
            skLineSegment(sketch, "E270", {"start": v(116.88, 103.4) * mm, "end": v(188.22, 84.84) * mm});
            skLineSegment(sketch, "E271", {"start": v(180.93, 102.44) * mm, "end": v(198, 109.5) * mm});
            skLineSegment(sketch, "E272", {"start": v(198, 109.5) * mm, "end": v(205.28, 91.9) * mm});
            skLineSegment(sketch, "E273", {"start": v(205.28, 91.9) * mm, "end": v(222.34, 98.97) * mm});
            skLineSegment(sketch, "E274", {"start": v(222.34, 98.97) * mm, "end": v(186.36, 185.83) * mm});
            skLineSegment(sketch, "E275", {"start": v(98.86, 222.07) * mm, "end": v(186.36, 185.83) * mm});
            skLineSegment(sketch, "E276", {"start": v(129.6, 116.13) * mm, "end": v(116.14, 129.6) * mm});
            skLineSegment(sketch, "E277", {"start": v(116.14, 129.6) * mm, "end": v(128.87, 142.34) * mm});
            skLineSegment(sketch, "E278.0", {"start": v(190.16, 126.88) * mm, "end": v(171.78, 171.25) * mm});
            skLineSegment(sketch, "E279.0", {"start": v(127, 190.43) * mm, "end": v(119.92, 173.35) * mm});
            skLineSegment(sketch, "E280.0", {"start": v(173.64, 120.04) * mm, "end": v(190.7, 127.1) * mm});
            skLineSegment(sketch, "E281", {"start": v(84.72, 187.94) * mm, "end": v(103.4, 116.88) * mm});
            skLineSegment(sketch, "E282", {"start": v(84.72, 187.94) * mm, "end": v(102.32, 180.64) * mm});
            skLineSegment(sketch, "E283", {"start": v(128.87, 142.34) * mm, "end": v(120.4, 174.52) * mm});
            skLineSegment(sketch, "E284", {"start": v(142.34, 128.86) * mm, "end": v(174.64, 120.45) * mm});
            skLineSegment(sketch, "E285.trimOffspring", {"start": v(126.77, 189.9) * mm, "end": v(171.78, 171.25) * mm});
            skSolve(sketch);
        }
        {
            var Q0;
            Q0=makeQuery(id+"F11.imprint","IMPRINT",FACE,{"disambiguationData":[TD([[makeQuery(id+"F11.imprint","IMPRINT",EDGE,{"derivedFrom":sQuery(id+"F11.wireOp",EDGE,"E264")}),1.0]])]});
            extrude(context, id + "F12", {"entities" : qUnion([Q0]), "depth" : 19.05 * mm});
        }
        {
            var Q0;
            Q0=sQuery(id+"F0.wireOp",EDGE,"E32");
            cPlane(context, id + "F13", {"entities" : qUnion([Q0]), "cplaneType" : CPlaneType.LINE_ANGLE, "offset" : 25.4 * mm, "angle" : 90 * degree, "width" : 152.4 * mm, "height" : 152.4 * mm});
        }
        {
            var Q0;
            Q0=qCreatedBy(id+"F13.planeOp",FACE);
            var sketch = newSketch(context, id + "F14", { "sketchPlane" : qUnion([Q0])});
            skLineSegment(sketch, "E286", {"start": v(207.84, 0) * mm, "end": v(207.84, 406.4) * mm, "construction": true});
            skLineSegment(sketch, "E287.MirrorCS", {"start": v(-323.87, 19.05) * mm, "end": v(-319.52, 19.05) * mm});
            skLineSegment(sketch, "E288.MirrorCS", {"start": v(-355.62, 387.35) * mm, "end": v(-355.62, 406.4) * mm});
            skLineSegment(sketch, "E289.MirrorCS", {"start": v(-355.62, 19.05) * mm, "end": v(-355.62, 0) * mm});
            skLineSegment(sketch, "E290.MirrorCS", {"start": v(-313.64, 406.4) * mm, "end": v(-355.62, 406.4) * mm});
            skLineSegment(sketch, "E291.MirrorCS", {"start": v(-355.62, 387.35) * mm, "end": v(207.84, 387.35) * mm, "construction": true});
            skLineSegment(sketch, "E292.MirrorCS", {"start": v(-355.62, 406.4) * mm, "end": v(207.84, 406.4) * mm, "construction": true});
            skLineSegment(sketch, "E293.MirrorCS", {"start": v(-355.62, 0) * mm, "end": v(-355.62, 406.4) * mm, "construction": true});
            skPoint(sketch, "E294.MirrorP", {"position": v(-355.62, 254) * mm});
            skLineSegment(sketch, "E295.MirrorCS", {"start": v(-313.64, 387.35) * mm, "end": v(-313.64, 406.4) * mm});
            skLineSegment(sketch, "E296.MirrorCS", {"start": v(-355.62, 0) * mm, "end": v(-323.87, 0) * mm});
            skLineSegment(sketch, "E297.MirrorCS", {"start": v(-240.25, 254) * mm, "end": v(-355.62, 387.35) * mm});
            skLineSegment(sketch, "E298.MirrorCS", {"start": v(-323.87, 19.05) * mm, "end": v(-323.87, 0) * mm});
            skLineSegment(sketch, "E299.MirrorCS", {"start": v(-355.62, 19.05) * mm, "end": v(-240.25, 234.95) * mm});
            skLineSegment(sketch, "E300.MirrorCS", {"start": v(-319.52, 19.05) * mm, "end": v(207.84, 19.05) * mm, "construction": true});
            skLineSegment(sketch, "E301.MirrorCS", {"start": v(-323.87, 0) * mm, "end": v(207.84, 0) * mm, "construction": true});
            skLineSegment(sketch, "E302.trimOffspring", {"start": v(-280.76, 91.77) * mm, "end": v(-204.25, 234.95) * mm});
            skLineSegment(sketch, "E303", {"start": v(-313.35, 30.79) * mm, "end": v(-319.52, 19.05) * mm});
            skLineSegment(sketch, "E304", {"start": v(-355.62, 254) * mm, "end": v(-240.25, 254) * mm, "construction": true});
            skLineSegment(sketch, "E305.0", {"start": v(-355.62, 234.95) * mm, "end": v(-204.25, 234.95) * mm, "construction": true});
            skLineSegment(sketch, "E306", {"start": v(-313.35, 30.79) * mm, "end": v(-9.53, 208.44) * mm});
            skLineSegment(sketch, "E307", {"start": v(-204.25, 234.95) * mm, "end": v(-204.25, 260.92) * mm});
            skLineSegment(sketch, "E308.trimOffspring", {"start": v(-204.25, 260.92) * mm, "end": v(-294.59, 365.33) * mm});
            skLineSegment(sketch, "E309.trimOffspring", {"start": v(-222.25, 254) * mm, "end": v(-35.41, 254) * mm, "construction": true});
            skLineSegment(sketch, "E310.trimOffspring", {"start": v(-204.25, 234.95) * mm, "end": v(-10.41, 234.95) * mm, "construction": true});
            skLineSegment(sketch, "E311", {"start": v(-240.25, 254) * mm, "end": v(-222.25, 254) * mm});
            skLineSegment(sketch, "E312", {"start": v(-222.25, 254) * mm, "end": v(-222.25, 234.95) * mm});
            skLineSegment(sketch, "E313", {"start": v(-222.25, 234.95) * mm, "end": v(-240.25, 234.95) * mm});
            skLineSegment(sketch, "E314", {"start": v(-0.89, 0) * mm, "end": v(-0.89, 406.4) * mm, "construction": true});
            skLineSegment(sketch, "E315", {"start": v(35.8, 234.95) * mm, "end": v(35.8, 254) * mm});
            skLineSegment(sketch, "E316", {"start": v(-10.41, 234.95) * mm, "end": v(-10.41, 254) * mm, "construction": true});
            skLineSegment(sketch, "E317", {"start": v(8.64, 234.95) * mm, "end": v(8.64, 254) * mm, "construction": true});
            skLineSegment(sketch, "E318.trimOffspring", {"start": v(35.8, 254) * mm, "end": v(207.84, 254) * mm, "construction": true});
            skLineSegment(sketch, "E319", {"start": v(-35.9, 254) * mm, "end": v(35.8, 254) * mm});
            skLineSegment(sketch, "E320.0", {"start": v(-280.76, 91.77) * mm, "end": v(-35.9, 234.95) * mm});
            skLineSegment(sketch, "E321", {"start": v(-35.9, 234.95) * mm, "end": v(-35.9, 254) * mm});
            skLineSegment(sketch, "E322", {"start": v(-9.53, 234.95) * mm, "end": v(9.52, 234.95) * mm});
            skLineSegment(sketch, "E323.trimOffspring", {"start": v(9.52, 219.58) * mm, "end": v(35.8, 234.95) * mm});
            skLineSegment(sketch, "E324", {"start": v(-9.53, 234.95) * mm, "end": v(-9.53, 208.44) * mm});
            skLineSegment(sketch, "E325", {"start": v(9.52, 234.95) * mm, "end": v(9.52, 219.58) * mm});
            skPoint(sketch, "E326", {"position": v(-294.59, 387.35) * mm});
            skLineSegment(sketch, "E327", {"start": v(-313.64, 387.35) * mm, "end": v(-294.59, 387.35) * mm});
            skLineSegment(sketch, "E328", {"start": v(-294.59, 387.35) * mm, "end": v(-294.59, 365.33) * mm});
            skSolve(sketch);
        }
        {
            var Q0;
            Q0=makeQuery(id+"F14.imprint","IMPRINT",FACE,{"disambiguationData":[TD([[makeQuery(id+"F14.imprint","IMPRINT",EDGE,{"derivedFrom":sQuery(id+"F14.wireOp",EDGE,"E287.MirrorCS")}),1.0]])]});
            extrude(context, id + "F15", {"entities" : qUnion([Q0]), "endBound" : BoundingType.SYMMETRIC, "depth" : 19.05 * mm});
        }
        {
            var Q0;
            Q0=sQuery(id+"F0.wireOp",EDGE,"E53");
            cPlane(context, id + "F16", {"entities" : qUnion([Q0]), "cplaneType" : CPlaneType.LINE_ANGLE, "offset" : 25.4 * mm, "angle" : 90 * degree, "width" : 152.4 * mm, "height" : 152.4 * mm});
        }
        {
            var Q0;
            Q0=qCreatedBy(id+"F16.planeOp",FACE);
            var sketch = newSketch(context, id + "F17", { "sketchPlane" : qUnion([Q0])});
            skLineSegment(sketch, "E329", {"start": v(228.88, 0) * mm, "end": v(228.88, 406.4) * mm, "construction": true});
            skLineSegment(sketch, "E330.MirrorCS", {"start": v(-7.6, 234.95) * mm, "end": v(-7.6, 254) * mm});
            skLineSegment(sketch, "E331.MirrorCS", {"start": v(-10.24, 406.4) * mm, "end": v(-43.1, 406.4) * mm});
            skLineSegment(sketch, "E332.MirrorCS", {"start": v(-136, 19.05) * mm, "end": v(-136, 0) * mm});
            skLineSegment(sketch, "E333.MirrorCS", {"start": v(-104.25, 19.05) * mm, "end": v(-99.05, 19.05) * mm});
            skLineSegment(sketch, "E334.MirrorCS", {"start": v(10.86, 234.95) * mm, "end": v(29.33, 234.95) * mm});
            skLineSegment(sketch, "E335.MirrorCS", {"start": v(84.13, 406.4) * mm, "end": v(46.44, 406.4) * mm});
            skLineSegment(sketch, "E336.MirrorCS", {"start": v(-136, 0) * mm, "end": v(-104.25, 0) * mm});
            skLineSegment(sketch, "E337.MirrorCS", {"start": v(46.44, 387.35) * mm, "end": v(46.44, 406.4) * mm});
            skLineSegment(sketch, "E338.MirrorCS", {"start": v(-104.25, 0) * mm, "end": v(-104.25, 19.05) * mm});
            skLineSegment(sketch, "E339.MirrorCS", {"start": v(-136, 406.4) * mm, "end": v(228.88, 406.4) * mm, "construction": true});
            skLineSegment(sketch, "E340.MirrorCS", {"start": v(6.42, 324.76) * mm, "end": v(-3.9, 363.5) * mm});
            skLineSegment(sketch, "E341.MirrorCS", {"start": v(-10.24, 387.35) * mm, "end": v(-10.24, 406.4) * mm});
            skLineSegment(sketch, "E342.MirrorCS", {"start": v(-136, 0) * mm, "end": v(-136, 406.4) * mm, "construction": true});
            skLineSegment(sketch, "E343.MirrorCS", {"start": v(10.86, 234.95) * mm, "end": v(228.88, 234.95) * mm, "construction": true});
            skLineSegment(sketch, "E344.MirrorCS", {"start": v(-43.1, 387.35) * mm, "end": v(-43.1, 406.4) * mm});
            skLineSegment(sketch, "E345.MirrorCS", {"start": v(95.04, 254) * mm, "end": v(228.88, 254) * mm, "construction": true});
            skLineSegment(sketch, "E346.MirrorCS", {"start": v(6.42, 324.76) * mm, "end": v(40.1, 377.42) * mm});
            skLineSegment(sketch, "E347.MirrorCS", {"start": v(-136, 387.35) * mm, "end": v(228.88, 387.35) * mm, "construction": true});
            skLineSegment(sketch, "E348.MirrorCS", {"start": v(-136, 0) * mm, "end": v(228.88, 0) * mm, "construction": true});
            skPoint(sketch, "E349.MirrorP", {"position": v(10.86, 234.95) * mm});
            skLineSegment(sketch, "E350.MirrorCS", {"start": v(-136, 19.05) * mm, "end": v(-7.6, 234.95) * mm});
            skLineSegment(sketch, "E351.MirrorCS", {"start": v(95.04, 0) * mm, "end": v(95.04, 406.4) * mm, "construction": true});
            skLineSegment(sketch, "E352.MirrorCS", {"start": v(-99.05, 19.05) * mm, "end": v(29.33, 234.95) * mm});
            skLineSegment(sketch, "E353.MirrorCS", {"start": v(-136, 254) * mm, "end": v(10.86, 254) * mm, "construction": true});
            skLineSegment(sketch, "E354.MirrorCS", {"start": v(-136, 234.95) * mm, "end": v(-7.6, 234.95) * mm, "construction": true});
            skLineSegment(sketch, "E355.MirrorCS", {"start": v(20.37, 287.65) * mm, "end": v(84.13, 387.35) * mm});
            skLineSegment(sketch, "E356.MirrorCS", {"start": v(-7.6, 254) * mm, "end": v(-43.1, 387.35) * mm});
            skLineSegment(sketch, "E357.MirrorCS", {"start": v(10.86, 234.95) * mm, "end": v(10.86, 254) * mm});
            skLineSegment(sketch, "E358.MirrorCS", {"start": v(84.13, 387.35) * mm, "end": v(84.13, 406.4) * mm});
            skLineSegment(sketch, "E359.MirrorCS", {"start": v(-134.63, 387.35) * mm, "end": v(230.24, 387.35) * mm, "construction": true});
            skLineSegment(sketch, "E360", {"start": v(29.33, 254) * mm, "end": v(20.37, 287.65) * mm});
            skLineSegment(sketch, "E361", {"start": v(10.86, 254) * mm, "end": v(29.33, 254) * mm});
            skPoint(sketch, "E362", {"position": v(-3.9, 387.35) * mm});
            skPoint(sketch, "E363", {"position": v(40.1, 387.35) * mm});
            skLineSegment(sketch, "E364", {"start": v(-10.24, 387.35) * mm, "end": v(-3.9, 387.35) * mm});
            skLineSegment(sketch, "E365", {"start": v(-3.9, 363.5) * mm, "end": v(-3.9, 387.35) * mm});
            skLineSegment(sketch, "E366", {"start": v(46.44, 387.35) * mm, "end": v(40.1, 387.35) * mm});
            skLineSegment(sketch, "E367", {"start": v(40.1, 377.42) * mm, "end": v(40.1, 387.35) * mm});
            skSolve(sketch);
        }
        {
            var Q0;
            Q0=makeQuery(id+"F17.imprint","IMPRINT",FACE,{"disambiguationData":[TD([[makeQuery(id+"F17.imprint","IMPRINT",EDGE,{"derivedFrom":sQuery(id+"F17.wireOp",EDGE,"E333.MirrorCS")}),1.0]])]});
            extrude(context, id + "F18", {"entities" : qUnion([Q0]), "endBound" : BoundingType.SYMMETRIC, "depth" : 19.05 * mm});
        }
        {
            var Q0;
            Q0=sQuery(id+"F0.wireOp",EDGE,"E54");
            cPlane(context, id + "F19", {"entities" : qUnion([Q0]), "cplaneType" : CPlaneType.LINE_ANGLE, "offset" : 25.4 * mm, "angle" : 0 * degree, "width" : 152.4 * mm, "height" : 152.4 * mm});
        }
        {
            var Q0;
            Q0=qCreatedBy(id+"F19.planeOp",FACE);
            var sketch = newSketch(context, id + "F20", { "sketchPlane" : qUnion([Q0])});
            skLineSegment(sketch, "E368", {"start": v(73.56, 0) * mm, "end": v(73.56, 406.4) * mm, "construction": true});
            skLineSegment(sketch, "E369.MirrorCS", {"start": v(406.69, 19.05) * mm, "end": v(401.5, 19.05) * mm});
            skLineSegment(sketch, "E370.MirrorCS", {"start": v(291.58, 234.95) * mm, "end": v(291.58, 254) * mm});
            skLineSegment(sketch, "E371.MirrorCS", {"start": v(218.31, 406.4) * mm, "end": v(256, 406.4) * mm});
            skLineSegment(sketch, "E372.MirrorCS", {"start": v(312.68, 406.4) * mm, "end": v(345.54, 406.4) * mm});
            skLineSegment(sketch, "E373.MirrorCS", {"start": v(438.44, 19.05) * mm, "end": v(438.44, 0) * mm});
            skLineSegment(sketch, "E374.MirrorCS", {"start": v(291.58, 234.95) * mm, "end": v(273.11, 234.95) * mm});
            skLineSegment(sketch, "E375.MirrorCS", {"start": v(438.44, 0) * mm, "end": v(406.69, 0) * mm});
            skLineSegment(sketch, "E376.MirrorCS", {"start": v(406.69, 0) * mm, "end": v(406.69, 19.05) * mm});
            skLineSegment(sketch, "E377.MirrorCS", {"start": v(438.44, 19.05) * mm, "end": v(310.05, 234.95) * mm});
            skLineSegment(sketch, "E378.MirrorCS", {"start": v(296.03, 324.76) * mm, "end": v(262.35, 377.42) * mm});
            skLineSegment(sketch, "E379.MirrorCS", {"start": v(438.44, 387.35) * mm, "end": v(73.56, 387.35) * mm, "construction": true});
            skLineSegment(sketch, "E380.MirrorCS", {"start": v(438.44, 234.95) * mm, "end": v(310.05, 234.95) * mm, "construction": true});
            skLineSegment(sketch, "E381.MirrorCS", {"start": v(310.05, 254) * mm, "end": v(345.54, 387.35) * mm});
            skLineSegment(sketch, "E382.MirrorCS", {"start": v(401.5, 19.05) * mm, "end": v(273.11, 234.95) * mm});
            skLineSegment(sketch, "E383.MirrorCS", {"start": v(282.07, 287.65) * mm, "end": v(218.31, 387.35) * mm});
            skPoint(sketch, "E384.MirrorP", {"position": v(291.58, 234.95) * mm});
            skLineSegment(sketch, "E385.MirrorCS", {"start": v(312.68, 387.35) * mm, "end": v(312.68, 406.4) * mm});
            skLineSegment(sketch, "E386.MirrorCS", {"start": v(310.05, 234.95) * mm, "end": v(310.05, 254) * mm});
            skLineSegment(sketch, "E387.MirrorCS", {"start": v(345.54, 387.35) * mm, "end": v(345.54, 406.4) * mm});
            skLineSegment(sketch, "E388.MirrorCS", {"start": v(218.31, 387.35) * mm, "end": v(218.31, 406.4) * mm});
            skLineSegment(sketch, "E389.MirrorCS", {"start": v(438.44, 0) * mm, "end": v(438.44, 406.4) * mm, "construction": true});
            skLineSegment(sketch, "E390.MirrorCS", {"start": v(291.58, 234.95) * mm, "end": v(73.56, 234.95) * mm, "construction": true});
            skLineSegment(sketch, "E391.MirrorCS", {"start": v(207.4, 0) * mm, "end": v(207.4, 406.4) * mm, "construction": true});
            skLineSegment(sketch, "E392.MirrorCS", {"start": v(438.44, 254) * mm, "end": v(291.58, 254) * mm, "construction": true});
            skLineSegment(sketch, "E393.MirrorCS", {"start": v(256, 387.35) * mm, "end": v(256, 406.4) * mm});
            skLineSegment(sketch, "E394.MirrorCS", {"start": v(438.44, 406.4) * mm, "end": v(73.56, 406.4) * mm, "construction": true});
            skLineSegment(sketch, "E395.MirrorCS", {"start": v(296.03, 324.76) * mm, "end": v(306.33, 363.49) * mm});
            skLineSegment(sketch, "E396.MirrorCS", {"start": v(438.44, 0) * mm, "end": v(73.56, 0) * mm, "construction": true});
            skLineSegment(sketch, "E397.MirrorCS", {"start": v(207.4, 254) * mm, "end": v(73.56, 254) * mm, "construction": true});
            skLineSegment(sketch, "E398.MirrorCS", {"start": v(436.67, 387.35) * mm, "end": v(71.8, 387.35) * mm, "construction": true});
            skLineSegment(sketch, "E399", {"start": v(273.11, 254) * mm, "end": v(282.07, 287.65) * mm});
            skLineSegment(sketch, "E400", {"start": v(291.58, 254) * mm, "end": v(273.11, 254) * mm});
            skPoint(sketch, "E401", {"position": v(262.35, 387.35) * mm});
            skPoint(sketch, "E402", {"position": v(306.33, 387.35) * mm});
            skLineSegment(sketch, "E403", {"start": v(256, 387.35) * mm, "end": v(262.35, 387.35) * mm});
            skLineSegment(sketch, "E404", {"start": v(262.35, 377.42) * mm, "end": v(262.35, 387.35) * mm});
            skLineSegment(sketch, "E405", {"start": v(306.33, 387.35) * mm, "end": v(306.33, 363.49) * mm});
            skLineSegment(sketch, "E406", {"start": v(306.33, 387.35) * mm, "end": v(312.68, 387.35) * mm});
            skSolve(sketch);
        }
        {
            var Q0;
            Q0 = qSketchRegion(id + "F20", true);
            extrude(context, id + "F21", {"entities" : qUnion([Q0]), "endBound" : BoundingType.SYMMETRIC, "depth" : 19.05 * mm});
        }
        {
            var Q0;
            Q0=makeQuery(id+"F15.opExtrude","SWEPT_FACE",FACE,{"disambiguationData":[OSD([sQuery(id+"F14.wireOp",EDGE,"E313")])]});
            cPlane(context, id + "F22", {"entities" : qUnion([Q0]), "cplaneType" : CPlaneType.OFFSET, "offset" : 0 * mm, "width" : 152.4 * mm, "height" : 152.4 * mm});
        }
        {
            var Q0;
            Q0=qCreatedBy(id+"F22.planeOp",FACE);
            var sketch = newSketch(context, id + "F23", { "sketchPlane" : qUnion([Q0])});
            skLineSegment(sketch, "E407", {"start": v(474.08, 188.1) * mm, "end": v(456.48, 180.8) * mm});
            skLineSegment(sketch, "E408", {"start": v(336.85, 98.74) * mm, "end": v(353.91, 91.67) * mm});
            skLineSegment(sketch, "E409", {"start": v(442.79, 129.49) * mm, "end": v(430.06, 142.22) * mm});
            skLineSegment(sketch, "E410", {"start": v(353.91, 91.67) * mm, "end": v(361.2, 109.27) * mm});
            skLineSegment(sketch, "E411", {"start": v(361.2, 109.27) * mm, "end": v(378.28, 102.2) * mm});
            skLineSegment(sketch, "E412", {"start": v(442.04, 103.3) * mm, "end": v(455.5, 116.76) * mm});
            skLineSegment(sketch, "E413", {"start": v(455.5, 116.76) * mm, "end": v(474.08, 188.1) * mm});
            skLineSegment(sketch, "E414", {"start": v(456.48, 180.8) * mm, "end": v(449.41, 197.87) * mm});
            skLineSegment(sketch, "E415", {"start": v(449.41, 197.87) * mm, "end": v(467.01, 205.17) * mm});
            skLineSegment(sketch, "E416", {"start": v(467.01, 205.17) * mm, "end": v(459.95, 222.22) * mm});
            skLineSegment(sketch, "E417", {"start": v(459.95, 222.22) * mm, "end": v(373.09, 186.24) * mm});
            skLineSegment(sketch, "E418", {"start": v(336.85, 98.74) * mm, "end": v(373.09, 186.24) * mm});
            skLineSegment(sketch, "E419", {"start": v(442.79, 129.49) * mm, "end": v(429.31, 116.02) * mm});
            skLineSegment(sketch, "E420", {"start": v(429.31, 116.02) * mm, "end": v(416.58, 128.75) * mm});
            skLineSegment(sketch, "E421.0", {"start": v(432.03, 190.04) * mm, "end": v(387.67, 171.66) * mm});
            skLineSegment(sketch, "E422.0", {"start": v(368.5, 126.87) * mm, "end": v(385.57, 119.8) * mm});
            skLineSegment(sketch, "E423.0", {"start": v(438.88, 173.52) * mm, "end": v(431.81, 190.58) * mm});
            skLineSegment(sketch, "E424", {"start": v(370.97, 84.6) * mm, "end": v(442.04, 103.3) * mm});
            skLineSegment(sketch, "E425", {"start": v(370.97, 84.6) * mm, "end": v(378.28, 102.2) * mm});
            skLineSegment(sketch, "E426", {"start": v(416.58, 128.75) * mm, "end": v(384.4, 120.29) * mm});
            skLineSegment(sketch, "E427", {"start": v(430.06, 142.22) * mm, "end": v(438.46, 174.52) * mm});
            skLineSegment(sketch, "E428.trimOffspring", {"start": v(369.03, 126.65) * mm, "end": v(387.67, 171.66) * mm});
            skSolve(sketch);
        }
        {
            var Q0;
            Q0=makeQuery(id+"F23.imprint","IMPRINT",FACE,{"disambiguationData":[TD([[makeQuery(id+"F23.imprint","IMPRINT",EDGE,{"derivedFrom":sQuery(id+"F23.wireOp",EDGE,"E407")}),1.0]])]});
            extrude(context, id + "F24", {"entities" : qUnion([Q0]), "depth" : 19.05 * mm});
        }
        {
            var Q0;
            Q0=makeQuery(id+"F0.imprint","IMPRINT",FACE,{"disambiguationData":[TD([[makeQuery(id+"F0.imprint","IMPRINT",EDGE,{"derivedFrom":sQuery(id+"F0.wireOp",EDGE,"E14")}),1.0]])]});
            extrude(context, id + "F25", {"entities" : qUnion([Q0]), "depth" : 19.05 * mm});
        }
        {
            var Q0;
            Q0=makeQuery(id+"F0.imprint","IMPRINT",FACE,{"disambiguationData":[TD([[makeQuery(id+"F0.imprint","IMPRINT",EDGE,{"derivedFrom":sQuery(id+"F0.wireOp",EDGE,"E39")}),1.0]])]});
            extrude(context, id + "F26", {"entities" : qUnion([Q0]), "depth" : 19.05 * mm});
        }
        {
            var Q0;
            {var subQ10=sQuery(id+"F0.wireOp",EDGE,"E84");Q0=makeQuery(id+"F0.imprint","IMPRINT",FACE,{"disambiguationData":[TD([[makeQuery(id+"F0.imprint","IMPRINT",EDGE,{"derivedFrom":subQ10}),1.0]])]});}
            extrude(context, id + "F27", {"entities" : qUnion([Q0]), "depth" : 19.05 * mm});
        }
        {
            var Q0;
            Q0=makeQuery(id+"F0.imprint","IMPRINT",FACE,{"disambiguationData":[TD([[makeQuery(id+"F0.imprint","IMPRINT",EDGE,{"derivedFrom":sQuery(id+"F0.wireOp",EDGE,"E118")}),-1.0]])]});
            extrude(context, id + "F28", {"entities" : qUnion([Q0]), "depth" : 19.05 * mm});
        }
        {
            var Q0;
            Q0=sQuery(id+"F0.wireOp",EDGE,"E8.MirrorCS");
            cPlane(context, id + "F29", {"entities" : qUnion([Q0]), "cplaneType" : CPlaneType.LINE_ANGLE, "offset" : 25.4 * mm, "angle" : 90 * degree, "width" : 152.4 * mm, "height" : 152.4 * mm});
        }
        {
            var Q0;
            Q0=qCreatedBy(id+"F29.planeOp",FACE);
            var sketch = newSketch(context, id + "F30", { "sketchPlane" : qUnion([Q0])});
            skLineSegment(sketch, "E429", {"start": v(187.02, 0) * mm, "end": v(187.02, 406.4) * mm, "construction": true});
            skLineSegment(sketch, "E430.MirrorCS", {"start": v(404.4, 234.95) * mm, "end": v(385.34, 234.95) * mm});
            skLineSegment(sketch, "E431.MirrorCS", {"start": v(635.11, 254) * mm, "end": v(617.11, 254) * mm});
            skLineSegment(sketch, "E432.MirrorCS", {"start": v(718.73, 19.05) * mm, "end": v(714.38, 19.05) * mm});
            skLineSegment(sketch, "E433.MirrorCS", {"start": v(750.48, 387.35) * mm, "end": v(750.48, 406.4) * mm});
            skLineSegment(sketch, "E434.MirrorCS", {"start": v(718.73, 19.05) * mm, "end": v(718.73, 0) * mm});
            skLineSegment(sketch, "E435.MirrorCS", {"start": v(750.48, 19.05) * mm, "end": v(750.48, 0) * mm});
            skLineSegment(sketch, "E436.MirrorCS", {"start": v(359.06, 234.95) * mm, "end": v(359.06, 254) * mm});
            skLineSegment(sketch, "E437.MirrorCS", {"start": v(617.11, 234.95) * mm, "end": v(635.11, 234.95) * mm});
            skLineSegment(sketch, "E438.MirrorCS", {"start": v(708.5, 387.35) * mm, "end": v(708.5, 406.4) * mm});
            skLineSegment(sketch, "E439.MirrorCS", {"start": v(385.34, 234.95) * mm, "end": v(385.34, 219.58) * mm});
            skLineSegment(sketch, "E440.MirrorCS", {"start": v(430.76, 234.95) * mm, "end": v(430.76, 254) * mm});
            skLineSegment(sketch, "E441.MirrorCS", {"start": v(617.11, 254) * mm, "end": v(617.11, 234.95) * mm});
            skLineSegment(sketch, "E442.MirrorCS", {"start": v(708.21, 30.79) * mm, "end": v(714.38, 19.05) * mm});
            skLineSegment(sketch, "E443.MirrorCS", {"start": v(386.22, 234.95) * mm, "end": v(386.22, 254) * mm, "construction": true});
            skLineSegment(sketch, "E444.MirrorCS", {"start": v(708.5, 406.4) * mm, "end": v(750.48, 406.4) * mm});
            skLineSegment(sketch, "E445.MirrorCS", {"start": v(405.27, 234.95) * mm, "end": v(405.27, 254) * mm, "construction": true});
            skLineSegment(sketch, "E446.MirrorCS", {"start": v(675.62, 91.77) * mm, "end": v(430.76, 234.95) * mm});
            skLineSegment(sketch, "E447.MirrorCS", {"start": v(750.48, 254) * mm, "end": v(635.11, 254) * mm, "construction": true});
            skLineSegment(sketch, "E448.MirrorCS", {"start": v(750.48, 387.35) * mm, "end": v(187.02, 387.35) * mm, "construction": true});
            skLineSegment(sketch, "E449.MirrorCS", {"start": v(750.48, 406.4) * mm, "end": v(187.02, 406.4) * mm, "construction": true});
            skLineSegment(sketch, "E450.MirrorCS", {"start": v(750.48, 19.05) * mm, "end": v(635.11, 234.95) * mm});
            skLineSegment(sketch, "E451.MirrorCS", {"start": v(359.06, 254) * mm, "end": v(187.02, 254) * mm, "construction": true});
            skLineSegment(sketch, "E452.MirrorCS", {"start": v(617.11, 254) * mm, "end": v(430.27, 254) * mm, "construction": true});
            skLineSegment(sketch, "E453.MirrorCS", {"start": v(708.21, 30.79) * mm, "end": v(404.4, 208.44) * mm});
            skLineSegment(sketch, "E454.MirrorCS", {"start": v(714.38, 19.05) * mm, "end": v(187.02, 19.05) * mm, "construction": true});
            skLineSegment(sketch, "E455.MirrorCS", {"start": v(718.73, 0) * mm, "end": v(187.02, 0) * mm, "construction": true});
            skLineSegment(sketch, "E456.MirrorCS", {"start": v(675.62, 91.77) * mm, "end": v(599.11, 234.95) * mm});
            skLineSegment(sketch, "E457.MirrorCS", {"start": v(750.48, 0) * mm, "end": v(750.48, 406.4) * mm, "construction": true});
            skLineSegment(sketch, "E458.MirrorCS", {"start": v(750.48, 0) * mm, "end": v(718.73, 0) * mm});
            skLineSegment(sketch, "E459.MirrorCS", {"start": v(635.11, 254) * mm, "end": v(750.48, 387.35) * mm});
            skLineSegment(sketch, "E460.MirrorCS", {"start": v(750.48, 234.95) * mm, "end": v(599.11, 234.95) * mm, "construction": true});
            skLineSegment(sketch, "E461.MirrorCS", {"start": v(385.34, 219.58) * mm, "end": v(359.06, 234.95) * mm});
            skLineSegment(sketch, "E462.MirrorCS", {"start": v(599.11, 234.95) * mm, "end": v(599.11, 260.92) * mm});
            skLineSegment(sketch, "E463.MirrorCS", {"start": v(395.75, 0) * mm, "end": v(395.75, 406.4) * mm, "construction": true});
            skLineSegment(sketch, "E464.MirrorCS", {"start": v(599.11, 234.95) * mm, "end": v(405.27, 234.95) * mm, "construction": true});
            skLineSegment(sketch, "E465.MirrorCS", {"start": v(430.76, 254) * mm, "end": v(359.06, 254) * mm});
            skLineSegment(sketch, "E466.MirrorCS", {"start": v(404.4, 234.95) * mm, "end": v(404.4, 208.44) * mm});
            skLineSegment(sketch, "E467.MirrorCS", {"start": v(599.11, 260.92) * mm, "end": v(689.43, 365.3) * mm});
            skPoint(sketch, "E468.MirrorP", {"position": v(750.48, 254) * mm});
            skLineSegment(sketch, "E469", {"start": v(708.5, 387.35) * mm, "end": v(689.43, 387.35) * mm});
            skLineSegment(sketch, "E470", {"start": v(689.43, 387.35) * mm, "end": v(689.43, 365.3) * mm});
            skSolve(sketch);
        }
        {
            var Q0;
            Q0=makeQuery(id+"F30.imprint","IMPRINT",FACE,{"disambiguationData":[TD([[makeQuery(id+"F30.imprint","IMPRINT",EDGE,{"derivedFrom":sQuery(id+"F30.wireOp",EDGE,"E430.MirrorCS")}),-1.0]])]});
            extrude(context, id + "F31", {"entities" : qUnion([Q0]), "endBound" : BoundingType.SYMMETRIC, "depth" : 19.05 * mm});
        }
        {
            var Q0;
            Q0=sQuery(id+"F0.wireOp",EDGE,"E113");
            cPlane(context, id + "F32", {"entities" : qUnion([Q0]), "cplaneType" : CPlaneType.LINE_ANGLE, "offset" : 25.4 * mm, "angle" : 90 * degree, "width" : 152.4 * mm, "height" : 152.4 * mm});
        }
        {
            var Q0;
            Q0=qCreatedBy(id+"F32.planeOp",FACE);
            var sketch = newSketch(context, id + "F33", { "sketchPlane" : qUnion([Q0])});
            skLineSegment(sketch, "E471", {"start": v(590, 0) * mm, "end": v(590, 406.4) * mm, "construction": true});
            skLineSegment(sketch, "E472.MirrorCS", {"start": v(923.13, 19.05) * mm, "end": v(917.93, 19.05) * mm});
            skLineSegment(sketch, "E473.MirrorCS", {"start": v(829.12, 406.4) * mm, "end": v(861.98, 406.4) * mm});
            skLineSegment(sketch, "E474.MirrorCS", {"start": v(808.02, 234.95) * mm, "end": v(789.55, 234.95) * mm});
            skLineSegment(sketch, "E475.MirrorCS", {"start": v(734.75, 406.4) * mm, "end": v(772.44, 406.4) * mm});
            skLineSegment(sketch, "E476.MirrorCS", {"start": v(954.87, 0) * mm, "end": v(923.13, 0) * mm});
            skLineSegment(sketch, "E477.MirrorCS", {"start": v(954.87, 19.05) * mm, "end": v(954.87, 0) * mm});
            skLineSegment(sketch, "E478.MirrorCS", {"start": v(861.98, 387.35) * mm, "end": v(861.98, 406.4) * mm});
            skLineSegment(sketch, "E479.MirrorCS", {"start": v(798.5, 287.65) * mm, "end": v(734.75, 387.35) * mm});
            skLineSegment(sketch, "E480.MirrorCS", {"start": v(954.87, 0) * mm, "end": v(590, 0) * mm, "construction": true});
            skLineSegment(sketch, "E481.MirrorCS", {"start": v(723.84, 0) * mm, "end": v(723.84, 406.4) * mm, "construction": true});
            skLineSegment(sketch, "E482.MirrorCS", {"start": v(954.87, 19.05) * mm, "end": v(826.49, 234.95) * mm});
            skLineSegment(sketch, "E483.MirrorCS", {"start": v(772.44, 387.35) * mm, "end": v(772.44, 406.4) * mm});
            skLineSegment(sketch, "E484.MirrorCS", {"start": v(954.87, 0) * mm, "end": v(954.87, 406.4) * mm, "construction": true});
            skLineSegment(sketch, "E485.MirrorCS", {"start": v(826.49, 234.95) * mm, "end": v(826.49, 254) * mm});
            skLineSegment(sketch, "E486.MirrorCS", {"start": v(808.02, 234.95) * mm, "end": v(590, 234.95) * mm, "construction": true});
            skLineSegment(sketch, "E487.MirrorCS", {"start": v(723.84, 254) * mm, "end": v(590, 254) * mm, "construction": true});
            skLineSegment(sketch, "E488.MirrorCS", {"start": v(812.46, 324.76) * mm, "end": v(778.78, 377.43) * mm});
            skLineSegment(sketch, "E489.MirrorCS", {"start": v(923.13, 0) * mm, "end": v(923.13, 19.05) * mm});
            skLineSegment(sketch, "E490.MirrorCS", {"start": v(829.12, 387.35) * mm, "end": v(829.12, 406.4) * mm});
            skLineSegment(sketch, "E491.MirrorCS", {"start": v(812.46, 324.76) * mm, "end": v(822.77, 363.5) * mm});
            skLineSegment(sketch, "E492.MirrorCS", {"start": v(917.93, 19.05) * mm, "end": v(789.55, 234.95) * mm});
            skLineSegment(sketch, "E493.MirrorCS", {"start": v(826.49, 254) * mm, "end": v(861.98, 387.35) * mm});
            skLineSegment(sketch, "E494.MirrorCS", {"start": v(808.02, 234.95) * mm, "end": v(808.02, 254) * mm});
            skLineSegment(sketch, "E495.MirrorCS", {"start": v(954.87, 387.35) * mm, "end": v(590, 387.35) * mm, "construction": true});
            skLineSegment(sketch, "E496.MirrorCS", {"start": v(954.87, 254) * mm, "end": v(808.02, 254) * mm, "construction": true});
            skLineSegment(sketch, "E497.MirrorCS", {"start": v(954.87, 234.95) * mm, "end": v(826.49, 234.95) * mm, "construction": true});
            skPoint(sketch, "E498.MirrorP", {"position": v(808.02, 234.95) * mm});
            skLineSegment(sketch, "E499.MirrorCS", {"start": v(954.87, 406.4) * mm, "end": v(590, 406.4) * mm, "construction": true});
            skLineSegment(sketch, "E500.MirrorCS", {"start": v(734.75, 387.35) * mm, "end": v(734.75, 406.4) * mm});
            skLineSegment(sketch, "E501.MirrorCS", {"start": v(789.55, 254) * mm, "end": v(798.5, 287.65) * mm});
            skLineSegment(sketch, "E502.MirrorCS", {"start": v(808.02, 254) * mm, "end": v(789.55, 254) * mm});
            skLineSegment(sketch, "E503", {"start": v(829.12, 387.35) * mm, "end": v(822.77, 387.35) * mm});
            skLineSegment(sketch, "E504", {"start": v(822.77, 387.35) * mm, "end": v(822.77, 363.5) * mm});
            skLineSegment(sketch, "E505", {"start": v(772.44, 387.35) * mm, "end": v(778.78, 387.35) * mm});
            skLineSegment(sketch, "E506", {"start": v(778.78, 387.35) * mm, "end": v(778.78, 377.43) * mm});
            skSolve(sketch);
        }
        {
            var Q0;
            Q0=makeQuery(id+"F33.imprint","IMPRINT",FACE,{"disambiguationData":[TD([[makeQuery(id+"F33.imprint","IMPRINT",EDGE,{"derivedFrom":sQuery(id+"F33.wireOp",EDGE,"E472.MirrorCS")}),-1.0]])]});
            extrude(context, id + "F34", {"entities" : qUnion([Q0]), "endBound" : BoundingType.SYMMETRIC, "depth" : 19.05 * mm});
        }
        {
            var Q0;
            Q0=sQuery(id+"F0.wireOp",EDGE,"E112");
            cPlane(context, id + "F35", {"entities" : qUnion([Q0]), "cplaneType" : CPlaneType.LINE_ANGLE, "offset" : 25.4 * mm, "angle" : 0 * degree, "width" : 152.4 * mm, "height" : 152.4 * mm});
        }
        {
            var Q0;
            Q0=qCreatedBy(id+"F35.planeOp",FACE);
            var sketch = newSketch(context, id + "F36", { "sketchPlane" : qUnion([Q0])});
            skLineSegment(sketch, "E507", {"start": v(-17.1, 0) * mm, "end": v(-17.1, 406.4) * mm, "construction": true});
            skLineSegment(sketch, "E508.MirrorCS", {"start": v(316.04, 19.05) * mm, "end": v(310.84, 19.05) * mm});
            skLineSegment(sketch, "E509.MirrorCS", {"start": v(222.03, 406.4) * mm, "end": v(254.89, 406.4) * mm});
            skLineSegment(sketch, "E510.MirrorCS", {"start": v(200.93, 234.95) * mm, "end": v(182.46, 234.95) * mm});
            skLineSegment(sketch, "E511.MirrorCS", {"start": v(127.66, 406.4) * mm, "end": v(165.35, 406.4) * mm});
            skLineSegment(sketch, "E512.MirrorCS", {"start": v(347.78, 0) * mm, "end": v(316.04, 0) * mm});
            skLineSegment(sketch, "E513.MirrorCS", {"start": v(347.78, 19.05) * mm, "end": v(347.78, 0) * mm});
            skLineSegment(sketch, "E514.MirrorCS", {"start": v(254.89, 387.35) * mm, "end": v(254.89, 406.4) * mm});
            skLineSegment(sketch, "E515.MirrorCS", {"start": v(191.42, 287.65) * mm, "end": v(127.66, 387.35) * mm});
            skLineSegment(sketch, "E516.MirrorCS", {"start": v(347.78, 0) * mm, "end": v(-17.1, 0) * mm, "construction": true});
            skLineSegment(sketch, "E517.MirrorCS", {"start": v(116.75, 0) * mm, "end": v(116.75, 406.4) * mm, "construction": true});
            skLineSegment(sketch, "E518.MirrorCS", {"start": v(347.78, 19.05) * mm, "end": v(219.4, 234.95) * mm});
            skLineSegment(sketch, "E519.MirrorCS", {"start": v(165.35, 387.35) * mm, "end": v(165.35, 406.4) * mm});
            skLineSegment(sketch, "E520.MirrorCS", {"start": v(347.78, 0) * mm, "end": v(347.78, 406.4) * mm, "construction": true});
            skLineSegment(sketch, "E521.MirrorCS", {"start": v(219.4, 234.95) * mm, "end": v(219.4, 254) * mm});
            skLineSegment(sketch, "E522.MirrorCS", {"start": v(200.93, 234.95) * mm, "end": v(-17.1, 234.95) * mm, "construction": true});
            skLineSegment(sketch, "E523.MirrorCS", {"start": v(116.75, 254) * mm, "end": v(-17.1, 254) * mm, "construction": true});
            skLineSegment(sketch, "E524.MirrorCS", {"start": v(205.37, 324.76) * mm, "end": v(171.7, 377.4) * mm});
            skLineSegment(sketch, "E525.MirrorCS", {"start": v(316.04, 0) * mm, "end": v(316.04, 19.05) * mm});
            skLineSegment(sketch, "E526.MirrorCS", {"start": v(222.03, 387.35) * mm, "end": v(222.03, 406.4) * mm});
            skLineSegment(sketch, "E527.MirrorCS", {"start": v(205.37, 324.76) * mm, "end": v(215.68, 363.48) * mm});
            skLineSegment(sketch, "E528.MirrorCS", {"start": v(310.84, 19.05) * mm, "end": v(182.46, 234.95) * mm});
            skLineSegment(sketch, "E529.MirrorCS", {"start": v(219.4, 254) * mm, "end": v(254.89, 387.35) * mm});
            skLineSegment(sketch, "E530.MirrorCS", {"start": v(200.93, 234.95) * mm, "end": v(200.93, 254) * mm});
            skLineSegment(sketch, "E531.MirrorCS", {"start": v(347.78, 387.35) * mm, "end": v(-17.1, 387.35) * mm, "construction": true});
            skLineSegment(sketch, "E532.MirrorCS", {"start": v(347.78, 254) * mm, "end": v(200.93, 254) * mm, "construction": true});
            skLineSegment(sketch, "E533.MirrorCS", {"start": v(347.78, 234.95) * mm, "end": v(219.4, 234.95) * mm, "construction": true});
            skPoint(sketch, "E534.MirrorP", {"position": v(200.93, 234.95) * mm});
            skLineSegment(sketch, "E535.MirrorCS", {"start": v(347.78, 406.4) * mm, "end": v(-17.1, 406.4) * mm, "construction": true});
            skLineSegment(sketch, "E536.MirrorCS", {"start": v(127.66, 387.35) * mm, "end": v(127.66, 406.4) * mm});
            skLineSegment(sketch, "E537.MirrorCS", {"start": v(182.46, 254) * mm, "end": v(191.42, 287.65) * mm});
            skLineSegment(sketch, "E538.MirrorCS", {"start": v(200.93, 254) * mm, "end": v(182.46, 254) * mm});
            skLineSegment(sketch, "E539", {"start": v(165.35, 387.35) * mm, "end": v(171.7, 387.35) * mm});
            skLineSegment(sketch, "E540", {"start": v(171.7, 387.35) * mm, "end": v(171.7, 377.4) * mm});
            skLineSegment(sketch, "E541", {"start": v(222.03, 387.35) * mm, "end": v(215.68, 387.35) * mm});
            skLineSegment(sketch, "E542", {"start": v(215.68, 387.35) * mm, "end": v(215.68, 363.48) * mm});
            skSolve(sketch);
        }
        {
            var Q0;
            Q0=makeQuery(id+"F36.imprint","IMPRINT",FACE,{"disambiguationData":[TD([[makeQuery(id+"F36.imprint","IMPRINT",EDGE,{"derivedFrom":sQuery(id+"F36.wireOp",EDGE,"E508.MirrorCS")}),-1.0]])]});
            extrude(context, id + "F37", {"entities" : qUnion([Q0]), "endBound" : BoundingType.SYMMETRIC, "depth" : 19.05 * mm});
        }
        {
            var Q0;
            Q0=sQuery(id+"F0.wireOp",EDGE,"E2");
            cPlane(context, id + "F38", {"entities" : qUnion([Q0]), "cplaneType" : CPlaneType.LINE_ANGLE, "offset" : 25.4 * mm, "angle" : 90 * degree, "width" : 152.4 * mm, "height" : 152.4 * mm});
        }
        {
            var Q0;
            Q0=qCreatedBy(id+"F38.planeOp",FACE);
            var sketch = newSketch(context, id + "F39", { "sketchPlane" : qUnion([Q0])});
            skLineSegment(sketch, "E543", {"start": v(582.32, 0) * mm, "end": v(582.32, 406.4) * mm, "construction": true});
            skLineSegment(sketch, "E544.MirrorCS", {"start": v(1114.03, 19.05) * mm, "end": v(1109.68, 19.05) * mm});
            skLineSegment(sketch, "E545.MirrorCS", {"start": v(1103.5, 30.79) * mm, "end": v(1109.68, 19.05) * mm});
            skLineSegment(sketch, "E546.MirrorCS", {"start": v(1145.78, 387.35) * mm, "end": v(1145.78, 406.4) * mm});
            skLineSegment(sketch, "E547.MirrorCS", {"start": v(1145.78, 19.05) * mm, "end": v(1145.78, 0) * mm});
            skLineSegment(sketch, "E548.MirrorCS", {"start": v(1103.8, 406.4) * mm, "end": v(1145.78, 406.4) * mm});
            skLineSegment(sketch, "E549.MirrorCS", {"start": v(1012.4, 234.95) * mm, "end": v(1030.4, 234.95) * mm});
            skLineSegment(sketch, "E550.MirrorCS", {"start": v(800.57, 234.95) * mm, "end": v(800.57, 254) * mm});
            skLineSegment(sketch, "E551.MirrorCS", {"start": v(781.52, 254) * mm, "end": v(781.52, 234.95) * mm});
            skLineSegment(sketch, "E552.MirrorCS", {"start": v(781.52, 234.95) * mm, "end": v(800.57, 234.95) * mm});
            skLineSegment(sketch, "E553.MirrorCS", {"start": v(1109.68, 19.05) * mm, "end": v(582.32, 19.05) * mm, "construction": true});
            skLineSegment(sketch, "E554.MirrorCS", {"start": v(1114.03, 0) * mm, "end": v(582.32, 0) * mm, "construction": true});
            skLineSegment(sketch, "E555.MirrorCS", {"start": v(1070.92, 91.77) * mm, "end": v(994.41, 234.95) * mm});
            skPoint(sketch, "E556.MirrorP", {"position": v(1145.78, 254) * mm});
            skLineSegment(sketch, "E557.MirrorCS", {"start": v(1145.78, 387.35) * mm, "end": v(582.32, 387.35) * mm, "construction": true});
            skLineSegment(sketch, "E558.MirrorCS", {"start": v(1103.8, 387.35) * mm, "end": v(1103.8, 406.4) * mm});
            skLineSegment(sketch, "E559.MirrorCS", {"start": v(1030.4, 254) * mm, "end": v(1145.78, 387.35) * mm});
            skLineSegment(sketch, "E560.MirrorCS", {"start": v(754.35, 234.95) * mm, "end": v(754.35, 254) * mm});
            skLineSegment(sketch, "E561.MirrorCS", {"start": v(781.52, 254) * mm, "end": v(754.35, 254) * mm});
            skLineSegment(sketch, "E562.MirrorCS", {"start": v(1145.78, 234.95) * mm, "end": v(994.41, 234.95) * mm, "construction": true});
            skLineSegment(sketch, "E563.MirrorCS", {"start": v(1145.78, 406.4) * mm, "end": v(582.32, 406.4) * mm, "construction": true});
            skLineSegment(sketch, "E564.MirrorCS", {"start": v(1070.92, 91.77) * mm, "end": v(826.06, 234.95) * mm});
            skLineSegment(sketch, "E565.MirrorCS", {"start": v(994.41, 260.92) * mm, "end": v(1084.74, 365.33) * mm});
            skLineSegment(sketch, "E566.MirrorCS", {"start": v(791.05, 0) * mm, "end": v(791.05, 406.4) * mm, "construction": true});
            skLineSegment(sketch, "E567.MirrorCS", {"start": v(781.52, 219.06) * mm, "end": v(781.52, 254) * mm, "construction": true});
            skLineSegment(sketch, "E568.MirrorCS", {"start": v(1145.78, 19.05) * mm, "end": v(1030.4, 234.95) * mm});
            skLineSegment(sketch, "E569.MirrorCS", {"start": v(994.41, 234.95) * mm, "end": v(582.32, 234.95) * mm, "construction": true});
            skLineSegment(sketch, "E570.MirrorCS", {"start": v(800.57, 207.93) * mm, "end": v(800.57, 254) * mm, "construction": true});
            skLineSegment(sketch, "E571.MirrorCS", {"start": v(1030.4, 254) * mm, "end": v(1012.4, 254) * mm});
            skLineSegment(sketch, "E572.MirrorCS", {"start": v(1145.78, 0) * mm, "end": v(1114.03, 0) * mm});
            skLineSegment(sketch, "E573.MirrorCS", {"start": v(1012.4, 254) * mm, "end": v(825.57, 254) * mm, "construction": true});
            skLineSegment(sketch, "E574.MirrorCS", {"start": v(1012.4, 254) * mm, "end": v(1012.4, 234.95) * mm});
            skLineSegment(sketch, "E575.MirrorCS", {"start": v(1103.5, 30.79) * mm, "end": v(754.35, 234.95) * mm});
            skLineSegment(sketch, "E576.MirrorCS", {"start": v(1145.78, 0) * mm, "end": v(1145.78, 406.4) * mm, "construction": true});
            skLineSegment(sketch, "E577.MirrorCS", {"start": v(994.41, 234.95) * mm, "end": v(994.41, 260.92) * mm});
            skLineSegment(sketch, "E578.MirrorCS", {"start": v(1145.78, 254) * mm, "end": v(1030.4, 254) * mm, "construction": true});
            skLineSegment(sketch, "E579.MirrorCS", {"start": v(754.35, 254) * mm, "end": v(582.32, 254) * mm, "construction": true});
            skLineSegment(sketch, "E580.MirrorCS", {"start": v(826.06, 254) * mm, "end": v(800.57, 254) * mm});
            skLineSegment(sketch, "E581.MirrorCS", {"start": v(826.06, 234.95) * mm, "end": v(826.06, 254) * mm});
            skLineSegment(sketch, "E582.MirrorCS", {"start": v(1114.03, 19.05) * mm, "end": v(1114.03, 0) * mm});
            skLineSegment(sketch, "E583", {"start": v(1103.8, 387.35) * mm, "end": v(1084.74, 387.35) * mm});
            skLineSegment(sketch, "E584", {"start": v(1084.74, 387.35) * mm, "end": v(1084.74, 365.33) * mm});
            skSolve(sketch);
        }
        {
            var Q0;
            Q0=makeQuery(id+"F39.imprint","IMPRINT",FACE,{"disambiguationData":[TD([[makeQuery(id+"F39.imprint","IMPRINT",EDGE,{"derivedFrom":sQuery(id+"F39.wireOp",EDGE,"E544.MirrorCS")}),-1.0]])]});
            extrude(context, id + "F40", {"entities" : qUnion([Q0]), "endBound" : BoundingType.SYMMETRIC, "depth" : 19.05 * mm});
        }
        {
            var Q0;
            Q0=sQuery(id+"F0.wireOp",EDGE,"E144");
            cPlane(context, id + "F41", {"entities" : qUnion([Q0]), "cplaneType" : CPlaneType.LINE_ANGLE, "offset" : 25.4 * mm, "angle" : 0 * degree, "width" : 152.4 * mm, "height" : 152.4 * mm});
        }
        {
            var Q0;
            Q0=qCreatedBy(id+"F41.planeOp",FACE);
            var sketch = newSketch(context, id + "F42", { "sketchPlane" : qUnion([Q0])});
            skLineSegment(sketch, "E585", {"start": v(501.19, 0) * mm, "end": v(501.19, 406.4) * mm, "construction": true});
            skLineSegment(sketch, "E586.MirrorCS", {"start": v(834.31, 19.05) * mm, "end": v(829.12, 19.05) * mm});
            skLineSegment(sketch, "E587.MirrorCS", {"start": v(740.3, 406.4) * mm, "end": v(773.16, 406.4) * mm});
            skLineSegment(sketch, "E588.MirrorCS", {"start": v(719.2, 234.95) * mm, "end": v(700.74, 234.95) * mm});
            skLineSegment(sketch, "E589.MirrorCS", {"start": v(645.94, 406.4) * mm, "end": v(683.62, 406.4) * mm});
            skLineSegment(sketch, "E590.MirrorCS", {"start": v(866.06, 0) * mm, "end": v(834.31, 0) * mm});
            skLineSegment(sketch, "E591.MirrorCS", {"start": v(866.06, 19.05) * mm, "end": v(866.06, 0) * mm});
            skLineSegment(sketch, "E592.MirrorCS", {"start": v(773.16, 387.35) * mm, "end": v(773.16, 406.4) * mm});
            skLineSegment(sketch, "E593.MirrorCS", {"start": v(709.7, 287.65) * mm, "end": v(645.94, 387.35) * mm});
            skLineSegment(sketch, "E594.MirrorCS", {"start": v(866.06, 0) * mm, "end": v(501.19, 0) * mm, "construction": true});
            skLineSegment(sketch, "E595.MirrorCS", {"start": v(635.03, 0) * mm, "end": v(635.03, 406.4) * mm, "construction": true});
            skLineSegment(sketch, "E596.MirrorCS", {"start": v(866.06, 19.05) * mm, "end": v(737.68, 234.95) * mm});
            skLineSegment(sketch, "E597.MirrorCS", {"start": v(683.62, 387.35) * mm, "end": v(683.62, 406.4) * mm});
            skLineSegment(sketch, "E598.MirrorCS", {"start": v(866.06, 0) * mm, "end": v(866.06, 406.4) * mm, "construction": true});
            skLineSegment(sketch, "E599.MirrorCS", {"start": v(737.68, 234.95) * mm, "end": v(737.68, 254) * mm});
            skLineSegment(sketch, "E600.MirrorCS", {"start": v(719.2, 234.95) * mm, "end": v(501.19, 234.95) * mm, "construction": true});
            skLineSegment(sketch, "E601.MirrorCS", {"start": v(635.03, 254) * mm, "end": v(501.19, 254) * mm, "construction": true});
            skLineSegment(sketch, "E602.MirrorCS", {"start": v(723.65, 324.76) * mm, "end": v(689.98, 377.4) * mm});
            skLineSegment(sketch, "E603.MirrorCS", {"start": v(834.31, 0) * mm, "end": v(834.31, 19.05) * mm});
            skLineSegment(sketch, "E604.MirrorCS", {"start": v(740.3, 387.35) * mm, "end": v(740.3, 406.4) * mm});
            skLineSegment(sketch, "E605.MirrorCS", {"start": v(723.65, 324.76) * mm, "end": v(733.96, 363.49) * mm});
            skLineSegment(sketch, "E606.MirrorCS", {"start": v(829.12, 19.05) * mm, "end": v(700.74, 234.95) * mm});
            skLineSegment(sketch, "E607.MirrorCS", {"start": v(737.68, 254) * mm, "end": v(773.16, 387.35) * mm});
            skLineSegment(sketch, "E608.MirrorCS", {"start": v(719.2, 234.95) * mm, "end": v(719.2, 254) * mm});
            skLineSegment(sketch, "E609.MirrorCS", {"start": v(866.06, 387.35) * mm, "end": v(501.19, 387.35) * mm, "construction": true});
            skLineSegment(sketch, "E610.MirrorCS", {"start": v(866.06, 254) * mm, "end": v(719.2, 254) * mm, "construction": true});
            skLineSegment(sketch, "E611.MirrorCS", {"start": v(866.06, 234.95) * mm, "end": v(737.68, 234.95) * mm, "construction": true});
            skPoint(sketch, "E612.MirrorP", {"position": v(719.2, 234.95) * mm});
            skLineSegment(sketch, "E613.MirrorCS", {"start": v(866.06, 406.4) * mm, "end": v(501.19, 406.4) * mm, "construction": true});
            skLineSegment(sketch, "E614.MirrorCS", {"start": v(645.94, 387.35) * mm, "end": v(645.94, 406.4) * mm});
            skLineSegment(sketch, "E615.MirrorCS", {"start": v(700.74, 254) * mm, "end": v(709.7, 287.65) * mm});
            skLineSegment(sketch, "E616.MirrorCS", {"start": v(719.2, 254) * mm, "end": v(700.74, 254) * mm});
            skLineSegment(sketch, "E617", {"start": v(740.3, 387.35) * mm, "end": v(733.96, 387.35) * mm});
            skLineSegment(sketch, "E618", {"start": v(733.96, 387.35) * mm, "end": v(733.96, 363.49) * mm});
            skLineSegment(sketch, "E619", {"start": v(683.62, 387.35) * mm, "end": v(689.98, 387.35) * mm});
            skLineSegment(sketch, "E620", {"start": v(689.98, 387.35) * mm, "end": v(689.98, 377.4) * mm});
            skSolve(sketch);
        }
        {
            var Q0;
            Q0=makeQuery(id+"F42.imprint","IMPRINT",FACE,{"disambiguationData":[TD([[makeQuery(id+"F42.imprint","IMPRINT",EDGE,{"derivedFrom":sQuery(id+"F42.wireOp",EDGE,"E586.MirrorCS")}),-1.0]])]});
            extrude(context, id + "F43", {"entities" : qUnion([Q0]), "endBound" : BoundingType.SYMMETRIC, "depth" : 19.05 * mm});
        }
        {
            var Q0;
            Q0=sQuery(id+"F0.wireOp",EDGE,"E143");
            cPlane(context, id + "F44", {"entities" : qUnion([Q0]), "cplaneType" : CPlaneType.LINE_ANGLE, "offset" : 25.4 * mm, "angle" : 90 * degree, "width" : 152.4 * mm, "height" : 152.4 * mm});
        }
        {
            var Q0;
            Q0=qCreatedBy(id+"F44.planeOp",FACE);
            var sketch = newSketch(context, id + "F45", { "sketchPlane" : qUnion([Q0])});
            skLineSegment(sketch, "E621", {"start": v(803.6, 0) * mm, "end": v(803.6, 406.4) * mm, "construction": true});
            skLineSegment(sketch, "E622.MirrorCS", {"start": v(1136.72, 19.05) * mm, "end": v(1131.53, 19.05) * mm});
            skLineSegment(sketch, "E623.MirrorCS", {"start": v(1042.72, 406.4) * mm, "end": v(1075.58, 406.4) * mm});
            skLineSegment(sketch, "E624.MirrorCS", {"start": v(1021.62, 234.95) * mm, "end": v(1003.15, 234.95) * mm});
            skLineSegment(sketch, "E625.MirrorCS", {"start": v(948.35, 406.4) * mm, "end": v(986.04, 406.4) * mm});
            skLineSegment(sketch, "E626.MirrorCS", {"start": v(1168.47, 0) * mm, "end": v(1136.72, 0) * mm});
            skLineSegment(sketch, "E627.MirrorCS", {"start": v(1168.47, 19.05) * mm, "end": v(1168.47, 0) * mm});
            skLineSegment(sketch, "E628.MirrorCS", {"start": v(1075.58, 387.35) * mm, "end": v(1075.58, 406.4) * mm});
            skLineSegment(sketch, "E629.MirrorCS", {"start": v(1012.1, 287.65) * mm, "end": v(948.35, 387.35) * mm});
            skLineSegment(sketch, "E630.MirrorCS", {"start": v(1168.47, 0) * mm, "end": v(803.6, 0) * mm, "construction": true});
            skLineSegment(sketch, "E631.MirrorCS", {"start": v(937.44, 0) * mm, "end": v(937.44, 406.4) * mm, "construction": true});
            skLineSegment(sketch, "E632.MirrorCS", {"start": v(1168.47, 19.05) * mm, "end": v(1040.09, 234.95) * mm});
            skLineSegment(sketch, "E633.MirrorCS", {"start": v(986.04, 387.35) * mm, "end": v(986.04, 406.4) * mm});
            skLineSegment(sketch, "E634.MirrorCS", {"start": v(1168.47, 0) * mm, "end": v(1168.47, 406.4) * mm, "construction": true});
            skLineSegment(sketch, "E635.MirrorCS", {"start": v(1040.09, 234.95) * mm, "end": v(1040.09, 254) * mm});
            skLineSegment(sketch, "E636.MirrorCS", {"start": v(1021.62, 234.95) * mm, "end": v(803.6, 234.95) * mm, "construction": true});
            skLineSegment(sketch, "E637.MirrorCS", {"start": v(937.44, 254) * mm, "end": v(803.6, 254) * mm, "construction": true});
            skLineSegment(sketch, "E638.MirrorCS", {"start": v(1026.06, 324.76) * mm, "end": v(992.38, 377.43) * mm});
            skLineSegment(sketch, "E639.MirrorCS", {"start": v(1136.72, 0) * mm, "end": v(1136.72, 19.05) * mm});
            skLineSegment(sketch, "E640.MirrorCS", {"start": v(1042.72, 387.35) * mm, "end": v(1042.72, 406.4) * mm});
            skLineSegment(sketch, "E641.MirrorCS", {"start": v(1026.06, 324.76) * mm, "end": v(1036.36, 363.45) * mm});
            skLineSegment(sketch, "E642.MirrorCS", {"start": v(1131.53, 19.05) * mm, "end": v(1003.15, 234.95) * mm});
            skLineSegment(sketch, "E643.MirrorCS", {"start": v(1040.09, 254) * mm, "end": v(1075.58, 387.35) * mm});
            skLineSegment(sketch, "E644.MirrorCS", {"start": v(1021.62, 234.95) * mm, "end": v(1021.62, 254) * mm});
            skLineSegment(sketch, "E645.MirrorCS", {"start": v(1168.47, 387.35) * mm, "end": v(803.6, 387.35) * mm, "construction": true});
            skLineSegment(sketch, "E646.MirrorCS", {"start": v(1168.47, 254) * mm, "end": v(1021.62, 254) * mm, "construction": true});
            skLineSegment(sketch, "E647.MirrorCS", {"start": v(1168.47, 234.95) * mm, "end": v(1040.09, 234.95) * mm, "construction": true});
            skPoint(sketch, "E648.MirrorP", {"position": v(1021.62, 234.95) * mm});
            skLineSegment(sketch, "E649.MirrorCS", {"start": v(1168.47, 406.4) * mm, "end": v(803.6, 406.4) * mm, "construction": true});
            skLineSegment(sketch, "E650.MirrorCS", {"start": v(948.35, 387.35) * mm, "end": v(948.35, 406.4) * mm});
            skLineSegment(sketch, "E651.MirrorCS", {"start": v(1003.15, 254) * mm, "end": v(1012.1, 287.65) * mm});
            skLineSegment(sketch, "E652.MirrorCS", {"start": v(1021.62, 254) * mm, "end": v(1003.15, 254) * mm});
            skLineSegment(sketch, "E653", {"start": v(986.04, 387.35) * mm, "end": v(992.38, 387.35) * mm});
            skLineSegment(sketch, "E654", {"start": v(992.38, 387.35) * mm, "end": v(992.38, 377.43) * mm});
            skLineSegment(sketch, "E655", {"start": v(1042.72, 387.35) * mm, "end": v(1036.36, 387.35) * mm});
            skLineSegment(sketch, "E656", {"start": v(1036.36, 387.35) * mm, "end": v(1036.36, 363.45) * mm});
            skSolve(sketch);
        }
        {
            var Q0;
            Q0=makeQuery(id+"F45.imprint","IMPRINT",FACE,{"disambiguationData":[TD([[makeQuery(id+"F45.imprint","IMPRINT",EDGE,{"derivedFrom":sQuery(id+"F45.wireOp",EDGE,"E622.MirrorCS")}),-1.0]])]});
            extrude(context, id + "F46", {"entities" : qUnion([Q0]), "endBound" : BoundingType.SYMMETRIC, "depth" : 19.05 * mm});
        }
        {
            var Q0;
            Q0=makeQuery(id+"F31.opExtrude","SWEPT_FACE",FACE,{"disambiguationData":[OSD([sQuery(id+"F30.wireOp",EDGE,"E437.MirrorCS")])]});
            cPlane(context, id + "F47", {"entities" : qUnion([Q0]), "cplaneType" : CPlaneType.OFFSET, "offset" : 0 * mm, "width" : 152.4 * mm, "height" : 152.4 * mm});
        }
        {
            var Q0;
            Q0=qCreatedBy(id+"F47.planeOp",FACE);
            var sketch = newSketch(context, id + "F48", { "sketchPlane" : qUnion([Q0])});
            skLineSegment(sketch, "E657", {"start": v(85.64, 928.6) * mm, "end": v(103.24, 935.89) * mm});
            skLineSegment(sketch, "E658", {"start": v(222.87, 1017.96) * mm, "end": v(205.8, 1025.03) * mm});
            skLineSegment(sketch, "E659", {"start": v(116.93, 987.2) * mm, "end": v(129.66, 974.48) * mm});
            skLineSegment(sketch, "E660", {"start": v(205.8, 1025.03) * mm, "end": v(198.52, 1007.42) * mm});
            skLineSegment(sketch, "E661", {"start": v(198.52, 1007.42) * mm, "end": v(181.44, 1014.5) * mm});
            skLineSegment(sketch, "E662", {"start": v(117.68, 1013.4) * mm, "end": v(104.21, 999.94) * mm});
            skLineSegment(sketch, "E663", {"start": v(104.21, 999.94) * mm, "end": v(85.64, 928.6) * mm});
            skLineSegment(sketch, "E664", {"start": v(103.24, 935.89) * mm, "end": v(110.31, 918.82) * mm});
            skLineSegment(sketch, "E665", {"start": v(110.31, 918.82) * mm, "end": v(92.7, 911.53) * mm});
            skLineSegment(sketch, "E666", {"start": v(92.7, 911.53) * mm, "end": v(99.77, 894.47) * mm});
            skLineSegment(sketch, "E667", {"start": v(99.77, 894.47) * mm, "end": v(186.63, 930.45) * mm});
            skLineSegment(sketch, "E668", {"start": v(222.87, 1017.96) * mm, "end": v(186.63, 930.45) * mm});
            skLineSegment(sketch, "E669", {"start": v(116.93, 987.2) * mm, "end": v(130.4, 1000.68) * mm});
            skLineSegment(sketch, "E670", {"start": v(130.4, 1000.68) * mm, "end": v(143.14, 987.95) * mm});
            skLineSegment(sketch, "E671.0", {"start": v(127.69, 926.66) * mm, "end": v(172.05, 945.03) * mm});
            skLineSegment(sketch, "E672.0", {"start": v(191.23, 989.82) * mm, "end": v(174.15, 996.9) * mm});
            skLineSegment(sketch, "E673.0", {"start": v(120.84, 943.18) * mm, "end": v(127.91, 926.11) * mm});
            skLineSegment(sketch, "E674", {"start": v(188.75, 1032.1) * mm, "end": v(117.68, 1013.4) * mm});
            skLineSegment(sketch, "E675", {"start": v(188.75, 1032.1) * mm, "end": v(181.44, 1014.5) * mm});
            skLineSegment(sketch, "E676", {"start": v(143.14, 987.95) * mm, "end": v(175.33, 996.41) * mm});
            skLineSegment(sketch, "E677", {"start": v(129.66, 974.48) * mm, "end": v(121.26, 942.18) * mm});
            skLineSegment(sketch, "E678.trimOffspring", {"start": v(190.7, 990.05) * mm, "end": v(172.05, 945.03) * mm});
            skSolve(sketch);
        }
        {
            var Q0;
            Q0=makeQuery(id+"F48.imprint","IMPRINT",FACE,{"disambiguationData":[TD([[makeQuery(id+"F48.imprint","IMPRINT",EDGE,{"derivedFrom":sQuery(id+"F48.wireOp",EDGE,"E657")}),1.0]])]});
            extrude(context, id + "F49", {"entities" : qUnion([Q0]), "depth" : 19.05 * mm});
        }
        {
            var Q0;
            Q0=makeQuery(id+"F40.opExtrude","SWEPT_FACE",FACE,{"disambiguationData":[OSD([sQuery(id+"F39.wireOp",EDGE,"E549.MirrorCS")])]});
            cPlane(context, id + "F50", {"entities" : qUnion([Q0]), "cplaneType" : CPlaneType.OFFSET, "offset" : 0 * mm, "width" : 152.4 * mm, "height" : 152.4 * mm});
        }
        {
            var Q0;
            Q0=qCreatedBy(id+"F50.planeOp",FACE);
            var sketch = newSketch(context, id + "F51", { "sketchPlane" : qUnion([Q0])});
            skLineSegment(sketch, "E679", {"start": v(371.13, 1033.5) * mm, "end": v(378.42, 1015.9) * mm});
            skLineSegment(sketch, "E680", {"start": v(460.5, 896.26) * mm, "end": v(467.56, 913.33) * mm});
            skLineSegment(sketch, "E681", {"start": v(429.74, 1002.2) * mm, "end": v(417, 989.47) * mm});
            skLineSegment(sketch, "E682", {"start": v(467.56, 913.33) * mm, "end": v(449.96, 920.62) * mm});
            skLineSegment(sketch, "E683", {"start": v(449.96, 920.62) * mm, "end": v(457.03, 937.7) * mm});
            skLineSegment(sketch, "E684", {"start": v(455.94, 1001.45) * mm, "end": v(442.47, 1014.92) * mm});
            skLineSegment(sketch, "E685", {"start": v(442.47, 1014.92) * mm, "end": v(371.13, 1033.5) * mm});
            skLineSegment(sketch, "E686", {"start": v(378.42, 1015.9) * mm, "end": v(361.36, 1008.82) * mm});
            skLineSegment(sketch, "E687", {"start": v(361.36, 1008.82) * mm, "end": v(354.07, 1026.43) * mm});
            skLineSegment(sketch, "E688", {"start": v(354.07, 1026.43) * mm, "end": v(337, 1019.36) * mm});
            skLineSegment(sketch, "E689", {"start": v(337, 1019.36) * mm, "end": v(372.99, 932.5) * mm});
            skLineSegment(sketch, "E690", {"start": v(460.5, 896.26) * mm, "end": v(372.99, 932.5) * mm});
            skLineSegment(sketch, "E691", {"start": v(429.74, 1002.2) * mm, "end": v(443.21, 988.72) * mm});
            skLineSegment(sketch, "E692", {"start": v(443.21, 988.72) * mm, "end": v(430.48, 976) * mm});
            skLineSegment(sketch, "E693.0", {"start": v(369.19, 991.45) * mm, "end": v(387.57, 947.08) * mm});
            skLineSegment(sketch, "E694.0", {"start": v(432.36, 927.9) * mm, "end": v(439.43, 944.98) * mm});
            skLineSegment(sketch, "E695.0", {"start": v(385.71, 998.3) * mm, "end": v(368.65, 991.22) * mm});
            skLineSegment(sketch, "E696", {"start": v(474.63, 930.39) * mm, "end": v(455.94, 1001.45) * mm});
            skLineSegment(sketch, "E697", {"start": v(474.63, 930.39) * mm, "end": v(457.03, 937.7) * mm});
            skLineSegment(sketch, "E698", {"start": v(430.48, 976) * mm, "end": v(438.94, 943.8) * mm});
            skLineSegment(sketch, "E699", {"start": v(417, 989.47) * mm, "end": v(384.7, 997.88) * mm});
            skLineSegment(sketch, "E700.trimOffspring", {"start": v(432.58, 928.44) * mm, "end": v(387.57, 947.08) * mm});
            skSolve(sketch);
        }
        {
            var Q0;
            Q0=makeQuery(id+"F51.imprint","IMPRINT",FACE,{"disambiguationData":[TD([[makeQuery(id+"F51.imprint","IMPRINT",EDGE,{"derivedFrom":sQuery(id+"F51.wireOp",EDGE,"E679")}),1.0]])]});
            extrude(context, id + "F52", {"entities" : qUnion([Q0]), "depth" : 19.05 * mm});
        }
        {
            var Q0;
            Q0=makeQuery(id+"F15.opExtrude","SWEPT_FACE",FACE,{"disambiguationData":[OSD([sQuery(id+"F14.wireOp",EDGE,"E319")])]});
            cPlane(context, id + "F53", {"entities" : qUnion([Q0]), "cplaneType" : CPlaneType.OFFSET, "offset" : 0 * mm, "width" : 152.4 * mm, "height" : 152.4 * mm});
        }
        {
            var Q0;
            Q0=qCreatedBy(id+"F53.planeOp",FACE);
            var sketch = newSketch(context, id + "F54", { "sketchPlane" : qUnion([Q0])});
            skLineSegment(sketch, "E701", {"start": v(279.52, 53.06) * mm, "end": v(279.52, 1160.5) * mm, "construction": true});
            skLineSegment(sketch, "E702", {"start": v(279.52, 265.8) * mm, "end": v(261.5, 247.78) * mm});
            skLineSegment(sketch, "E703", {"start": v(261.5, 247.78) * mm, "end": v(248.02, 261.26) * mm});
            skLineSegment(sketch, "E704", {"start": v(248.02, 261.26) * mm, "end": v(266.04, 279.28) * mm});
            skLineSegment(sketch, "E705", {"start": v(266.04, 279.28) * mm, "end": v(247.34, 297.98) * mm});
            skLineSegment(sketch, "E706", {"start": v(247.34, 297.98) * mm, "end": v(260.81, 311.46) * mm});
            skLineSegment(sketch, "E707", {"start": v(260.81, 311.46) * mm, "end": v(279.52, 292.75) * mm});
            skLineSegment(sketch, "E708", {"start": v(279.52, 292.75) * mm, "end": v(298.73, 311.96) * mm});
            skLineSegment(sketch, "E709", {"start": v(298.73, 311.96) * mm, "end": v(312.2, 298.49) * mm});
            skLineSegment(sketch, "E710", {"start": v(312.2, 298.49) * mm, "end": v(293, 279.28) * mm});
            skLineSegment(sketch, "E711", {"start": v(293, 279.28) * mm, "end": v(311.52, 260.75) * mm});
            skLineSegment(sketch, "E712", {"start": v(311.52, 260.75) * mm, "end": v(298.05, 247.27) * mm});
            skLineSegment(sketch, "E713", {"start": v(298.05, 247.27) * mm, "end": v(279.52, 265.8) * mm});
            skLineSegment(sketch, "E714", {"start": v(279.49, 824.63) * mm, "end": v(261.47, 806.61) * mm});
            skLineSegment(sketch, "E715", {"start": v(261.47, 806.61) * mm, "end": v(248, 820.08) * mm});
            skLineSegment(sketch, "E716", {"start": v(248, 820.08) * mm, "end": v(266.01, 838.1) * mm});
            skLineSegment(sketch, "E717", {"start": v(266.01, 838.1) * mm, "end": v(247.3, 856.8) * mm});
            skLineSegment(sketch, "E718", {"start": v(247.3, 856.8) * mm, "end": v(260.78, 870.28) * mm});
            skLineSegment(sketch, "E719", {"start": v(260.78, 870.28) * mm, "end": v(279.49, 851.58) * mm});
            skLineSegment(sketch, "E720", {"start": v(279.49, 851.58) * mm, "end": v(298.7, 870.8) * mm});
            skLineSegment(sketch, "E721", {"start": v(298.7, 870.8) * mm, "end": v(312.17, 857.32) * mm});
            skLineSegment(sketch, "E722", {"start": v(312.17, 857.32) * mm, "end": v(292.96, 838.1) * mm});
            skLineSegment(sketch, "E723", {"start": v(292.96, 838.1) * mm, "end": v(311.5, 819.58) * mm});
            skLineSegment(sketch, "E724", {"start": v(311.5, 819.58) * mm, "end": v(298.02, 806.1) * mm});
            skLineSegment(sketch, "E725", {"start": v(298.02, 806.1) * mm, "end": v(279.49, 824.63) * mm});
            skLineSegment(sketch, "E726", {"start": v(266.01, 838.1) * mm, "end": v(292.96, 838.1) * mm, "construction": true});
            skCircle(sketch, "E727.cCircle", {"center": v(279.52, 838.1) * mm, "radius": 50.11 * mm, "construction": true});
            skLineSegment(sketch, "E727.0", {"start": v(229.4, 809.17) * mm, "end": v(229.4, 867.04) * mm});
            skLineSegment(sketch, "E727.1", {"start": v(229.4, 867.04) * mm, "end": v(279.52, 895.97) * mm});
            skLineSegment(sketch, "E727.2", {"start": v(279.52, 895.97) * mm, "end": v(329.63, 867.04) * mm});
            skLineSegment(sketch, "E727.3", {"start": v(329.63, 867.04) * mm, "end": v(329.63, 809.17) * mm});
            skPoint(sketch, "E727.0.midPoint", {"position": v(229.4, 838.1) * mm});
            skCircle(sketch, "E728.cCircle", {"center": v(279.54, 279.28) * mm, "radius": 50.11 * mm, "construction": true});
            skLineSegment(sketch, "E728.0", {"start": v(229.43, 250.35) * mm, "end": v(229.43, 308.21) * mm});
            skLineSegment(sketch, "E728.1", {"start": v(244.18, 316.73) * mm, "end": v(287.2, 341.57) * mm, "construction": true});
            skLineSegment(sketch, "E728.2", {"start": v(272.22, 341.37) * mm, "end": v(315.22, 316.55) * mm, "construction": true});
            skLineSegment(sketch, "E728.3", {"start": v(329.65, 308.21) * mm, "end": v(329.65, 250.35) * mm});
            skLineSegment(sketch, "E728.4", {"start": v(329.65, 250.35) * mm, "end": v(279.54, 221.42) * mm});
            skLineSegment(sketch, "E728.5", {"start": v(279.54, 221.42) * mm, "end": v(229.43, 250.35) * mm});
            skLineSegment(sketch, "E729", {"start": v(293, 279.28) * mm, "end": v(214.17, 279.28) * mm, "construction": true});
            skLineSegment(sketch, "E730", {"start": v(329.63, 320.89) * mm, "end": v(329.65, 320.89) * mm});
            skLineSegment(sketch, "E731.0", {"start": v(304.92, 279) * mm, "end": v(304.92, 279) * mm});
            skLineSegment(sketch, "E732.0", {"start": v(254.12, 279.02) * mm, "end": v(254.12, 279.03) * mm});
            skLineSegment(sketch, "E733.trimOffspring", {"start": v(254.12, 365.4) * mm, "end": v(254.12, 365.4) * mm});
            skLineSegment(sketch, "E734.trimOffspring", {"start": v(279.52, 580.1) * mm, "end": v(279.53, 580.16) * mm});
            skLineSegment(sketch, "E735.trimOffspring", {"start": v(279.53, 580.16) * mm, "end": v(279.52, 580.2) * mm});
            skLineSegment(sketch, "E736.trimOffspring", {"start": v(254.12, 794.9) * mm, "end": v(254.12, 794.9) * mm});
            skLineSegment(sketch, "E737.trimOffspring", {"start": v(304.92, 794.9) * mm, "end": v(304.92, 794.9) * mm});
            skLineSegment(sketch, "E738.trimOffspring", {"start": v(254.12, 881.3) * mm, "end": v(254.12, 881.3) * mm});
            skLineSegment(sketch, "E739.trimOffspring", {"start": v(304.92, 881.3) * mm, "end": v(304.92, 881.3) * mm});
            skLineSegment(sketch, "E740", {"start": v(260.81, 311.46) * mm, "end": v(261.47, 806.61) * mm, "construction": true});
            skLineSegment(sketch, "E741", {"start": v(298.73, 311.96) * mm, "end": v(298.02, 806.1) * mm, "construction": true});
            skPoint(sketch, "E742", {"position": v(261.14, 559.03) * mm});
            skLineSegment(sketch, "E743", {"start": v(279.52, 559.06) * mm, "end": v(203.32, 558.95) * mm, "construction": true});
            skLineSegment(sketch, "E744", {"start": v(203.32, 558.95) * mm, "end": v(244.18, 316.73) * mm});
            skLineSegment(sketch, "E745", {"start": v(279.52, 559.06) * mm, "end": v(355.72, 559.17) * mm, "construction": true});
            skLineSegment(sketch, "E746", {"start": v(355.72, 559.17) * mm, "end": v(315.22, 316.55) * mm});
            skLineSegment(sketch, "E747", {"start": v(203.32, 558.95) * mm, "end": v(244.62, 800.39) * mm});
            skLineSegment(sketch, "E748.0", {"start": v(235.52, 558.91) * mm, "end": v(272.72, 776.32) * mm});
            skLineSegment(sketch, "E749.0", {"start": v(323.52, 559.12) * mm, "end": v(287.2, 341.57) * mm});
            skLineSegment(sketch, "E750.0", {"start": v(235.5, 559) * mm, "end": v(272.22, 341.37) * mm});
            skLineSegment(sketch, "E751", {"start": v(244.62, 800.39) * mm, "end": v(279.52, 780.24) * mm, "construction": true});
            skLineSegment(sketch, "E752", {"start": v(279.52, 780.24) * mm, "end": v(314.72, 800.57) * mm, "construction": true});
            skPoint(sketch, "E753.orphan", {"position": v(279.54, 337.15) * mm});
            skLineSegment(sketch, "E754", {"start": v(244.18, 316.73) * mm, "end": v(229.43, 308.21) * mm});
            skLineSegment(sketch, "E755", {"start": v(315.22, 316.55) * mm, "end": v(329.65, 308.21) * mm});
            skLineSegment(sketch, "E756", {"start": v(279.54, 337.15) * mm, "end": v(272.22, 341.37) * mm});
            skLineSegment(sketch, "E757", {"start": v(279.54, 337.15) * mm, "end": v(287.2, 341.57) * mm});
            skLineSegment(sketch, "E758", {"start": v(329.63, 809.17) * mm, "end": v(314.72, 800.57) * mm});
            skLineSegment(sketch, "E759", {"start": v(244.62, 800.39) * mm, "end": v(229.4, 809.17) * mm});
            skLineSegment(sketch, "E760", {"start": v(279.52, 780.24) * mm, "end": v(272.72, 776.32) * mm});
            skLineSegment(sketch, "E761", {"start": v(279.52, 780.24) * mm, "end": v(286.67, 776.11) * mm});
            skLineSegment(sketch, "E762.trimOffspring", {"start": v(286.67, 776.11) * mm, "end": v(323.52, 559.12) * mm});
            skLineSegment(sketch, "E763.trimOffspring", {"start": v(314.72, 800.57) * mm, "end": v(355.72, 559.17) * mm});
            skSolve(sketch);
        }
        {
            var Q0;
            Q0=makeQuery(id+"F54.imprint","IMPRINT",FACE,{"disambiguationData":[TD([[makeQuery(id+"F54.imprint","IMPRINT",EDGE,{"derivedFrom":sQuery(id+"F54.wireOp",EDGE,"E702")}),1.0]])]});
            var Q1;
            {var subQ0=sQuery(id+"F54.wireOp",EDGE,"l7EIQis9-FzFm-eCiB-VRdT-U6j2Lq1q2NR1");Q1=makeQuery(id+"F54.imprint","IMPRINT",FACE,{"disambiguationData":[TD([[makeQuery(id+"F54.imprint","IMPRINT",EDGE,{"derivedFrom":subQ0}),-1.0]])]});}
            var Q2;
            {var subQ10=sQuery(id+"F54.wireOp",EDGE,"E705");Q2=makeQuery(id+"F54.imprint","IMPRINT",FACE,{"disambiguationData":[TD([[makeQuery(id+"F54.imprint","IMPRINT",EDGE,{"derivedFrom":subQ10}),1.0]])]});}
            extrude(context, id + "F55", {"entities" : qUnion([Q0, Q1, Q2]), "oppositeDirection" : true, "depth" : 19.05 * mm});
        }
        {
            var Q0;
            Q0=makeQuery(id+"F0.imprint","IMPRINT",FACE,{"disambiguationData":[TD([[makeQuery(id+"F0.imprint","IMPRINT",EDGE,{"derivedFrom":sQuery(id+"F0.wireOp",EDGE,"E0.bottom")}),-1.0]])]});
            cPlane(context, id + "F56", {"entities" : qUnion([Q0]), "cplaneType" : CPlaneType.OFFSET, "offset" : 387.35 * mm, "width" : 152.4 * mm, "height" : 152.4 * mm});
        }
        {
            var Q0;
            Q0=qCreatedBy(id+"F56.planeOp",FACE);
            var sketch = newSketch(context, id + "F57", { "sketchPlane" : qUnion([Q0])});
            skLineSegment(sketch, "E764", {"start": v(537.6, 34.67) * mm, "end": v(524.12, 21.2) * mm});
            skLineSegment(sketch, "E765", {"start": v(524.12, 21.2) * mm, "end": v(494.44, 50.89) * mm});
            skLineSegment(sketch, "E766", {"start": v(35.42, 21.7) * mm, "end": v(65.1, 51.4) * mm});
            skLineSegment(sketch, "E767", {"start": v(65.1, 51.4) * mm, "end": v(51.63, 64.87) * mm});
            skLineSegment(sketch, "E768", {"start": v(51.63, 64.87) * mm, "end": v(21.94, 35.17) * mm});
            skLineSegment(sketch, "E769", {"start": v(21.94, 35.17) * mm, "end": v(35.42, 21.7) * mm});
            skLineSegment(sketch, "E770", {"start": v(507.99, 1053.1) * mm, "end": v(537.68, 1082.78) * mm});
            skLineSegment(sketch, "E771", {"start": v(537.68, 1082.78) * mm, "end": v(524.21, 1096.25) * mm});
            skLineSegment(sketch, "E772", {"start": v(524.21, 1096.25) * mm, "end": v(494.52, 1066.56) * mm});
            skLineSegment(sketch, "E773", {"start": v(494.52, 1066.56) * mm, "end": v(507.99, 1053.1) * mm});
            skLineSegment(sketch, "E774", {"start": v(64.52, 1066.55) * mm, "end": v(34.83, 1096.24) * mm});
            skLineSegment(sketch, "E775", {"start": v(34.83, 1096.24) * mm, "end": v(21.36, 1082.77) * mm});
            skLineSegment(sketch, "E776", {"start": v(21.36, 1082.77) * mm, "end": v(51.05, 1053.08) * mm});
            skLineSegment(sketch, "E777", {"start": v(51.05, 1053.08) * mm, "end": v(64.52, 1066.55) * mm});
            skLineSegment(sketch, "E778", {"start": v(494.44, 50.89) * mm, "end": v(507.9, 64.36) * mm});
            skLineSegment(sketch, "E779", {"start": v(537.6, 34.67) * mm, "end": v(507.9, 64.36) * mm});
            skPoint(sketch, "E780", {"position": v(530.86, 27.93) * mm});
            skLineSegment(sketch, "E781", {"start": v(530.86, 27.93) * mm, "end": v(558.8, 0) * mm, "construction": true});
            skPoint(sketch, "E782", {"position": v(28.68, 28.44) * mm});
            skLineSegment(sketch, "E783", {"start": v(28.68, 28.44) * mm, "end": v(0.76, 0.5) * mm, "construction": true});
            skPoint(sketch, "E784", {"position": v(530.95, 1089.52) * mm});
            skLineSegment(sketch, "E785", {"start": v(530.95, 1089.52) * mm, "end": v(558.89, 1117.45) * mm, "construction": true});
            skPoint(sketch, "E786", {"position": v(28.1, 1089.5) * mm});
            skLineSegment(sketch, "E787", {"start": v(28.1, 1089.5) * mm, "end": v(0.16, 1117.44) * mm, "construction": true});
            skLineSegment(sketch, "E788", {"start": v(35.98, 1117.44) * mm, "end": v(116.54, 1117.44) * mm});
            skLineSegment(sketch, "E789", {"start": v(558.88, 1081.62) * mm, "end": v(558.87, 868.54) * mm});
            skLineSegment(sketch, "E790", {"start": v(487.69, 962.17) * mm, "end": v(470.09, 969.47) * mm});
            skLineSegment(sketch, "E791", {"start": v(470.09, 969.47) * mm, "end": v(457.5, 939.11) * mm});
            skLineSegment(sketch, "E792", {"start": v(457.5, 939.11) * mm, "end": v(475.1, 931.82) * mm});
            skLineSegment(sketch, "E793", {"start": v(373.22, 1033.71) * mm, "end": v(380.51, 1016.1) * mm});
            skLineSegment(sketch, "E794", {"start": v(403.58, 1046.28) * mm, "end": v(410.87, 1028.68) * mm});
            skLineSegment(sketch, "E795", {"start": v(487.69, 962.17) * mm, "end": v(475.1, 931.82) * mm});
            skLineSegment(sketch, "E796", {"start": v(453.41, 879.46) * mm, "end": v(438.98, 844.64) * mm});
            skLineSegment(sketch, "E797", {"start": v(438.98, 844.64) * mm, "end": v(421.38, 851.93) * mm});
            skLineSegment(sketch, "E798", {"start": v(421.38, 851.93) * mm, "end": v(435.81, 886.75) * mm});
            skLineSegment(sketch, "E799", {"start": v(453.41, 879.46) * mm, "end": v(435.81, 886.75) * mm});
            skLineSegment(sketch, "E800", {"start": v(328.14, 994.42) * mm, "end": v(320.85, 1012.03) * mm});
            skLineSegment(sketch, "E801", {"start": v(284.82, 1000.54) * mm, "end": v(293.32, 980) * mm});
            skLineSegment(sketch, "E802", {"start": v(239.38, 1011.68) * mm, "end": v(232.1, 994.07) * mm});
            skLineSegment(sketch, "E803", {"start": v(232.1, 994.07) * mm, "end": v(266.93, 979.67) * mm});
            skLineSegment(sketch, "E804", {"start": v(266.93, 979.67) * mm, "end": v(274.2, 997.28) * mm});
            skLineSegment(sketch, "E805", {"start": v(239.38, 1011.68) * mm, "end": v(274.2, 997.28) * mm});
            skLineSegment(sketch, "E806", {"start": v(187, 1033.34) * mm, "end": v(156.63, 1045.9) * mm});
            skLineSegment(sketch, "E807", {"start": v(156.63, 1045.9) * mm, "end": v(149.35, 1028.29) * mm});
            skLineSegment(sketch, "E808", {"start": v(149.35, 1028.29) * mm, "end": v(179.71, 1015.73) * mm});
            skLineSegment(sketch, "E809", {"start": v(187, 1033.34) * mm, "end": v(179.71, 1015.73) * mm});
            skLineSegment(sketch, "E810", {"start": v(88.8, 969.57) * mm, "end": v(71.2, 962.29) * mm});
            skLineSegment(sketch, "E811", {"start": v(71.2, 962.29) * mm, "end": v(83.75, 931.93) * mm});
            skLineSegment(sketch, "E812", {"start": v(83.75, 931.93) * mm, "end": v(101.36, 939.2) * mm});
            skLineSegment(sketch, "E813", {"start": v(88.8, 969.57) * mm, "end": v(101.36, 939.2) * mm});
            skLineSegment(sketch, "E814", {"start": v(123.03, 886.83) * mm, "end": v(105.42, 879.55) * mm});
            skLineSegment(sketch, "E815", {"start": v(105.42, 879.55) * mm, "end": v(119.83, 844.72) * mm});
            skLineSegment(sketch, "E816", {"start": v(119.83, 844.72) * mm, "end": v(137.44, 852) * mm});
            skLineSegment(sketch, "E817", {"start": v(123.03, 886.83) * mm, "end": v(137.44, 852) * mm});
            skLineSegment(sketch, "E818", {"start": v(403.58, 1046.28) * mm, "end": v(373.22, 1033.71) * mm});
            skLineSegment(sketch, "E819", {"start": v(380.51, 1016.1) * mm, "end": v(410.87, 1028.68) * mm});
            skLineSegment(sketch, "E820", {"start": v(328.14, 994.42) * mm, "end": v(293.32, 980) * mm});
            skLineSegment(sketch, "E821", {"start": v(320.85, 1012.03) * mm, "end": v(286.03, 997.6) * mm});
            skLineSegment(sketch, "E822", {"start": v(470.05, 148.04) * mm, "end": v(487.66, 155.34) * mm});
            skLineSegment(sketch, "E823", {"start": v(487.66, 155.34) * mm, "end": v(475.08, 185.7) * mm});
            skLineSegment(sketch, "E824", {"start": v(475.08, 185.7) * mm, "end": v(457.48, 178.4) * mm});
            skLineSegment(sketch, "E825", {"start": v(470.05, 148.04) * mm, "end": v(457.48, 178.4) * mm});
            skLineSegment(sketch, "E826", {"start": v(435.79, 230.77) * mm, "end": v(453.4, 238.06) * mm});
            skLineSegment(sketch, "E827", {"start": v(453.4, 238.06) * mm, "end": v(438.97, 272.88) * mm});
            skLineSegment(sketch, "E828", {"start": v(438.97, 272.88) * mm, "end": v(421.37, 265.6) * mm});
            skLineSegment(sketch, "E829", {"start": v(435.79, 230.77) * mm, "end": v(421.37, 265.6) * mm});
            skLineSegment(sketch, "E830", {"start": v(403.5, 71.08) * mm, "end": v(410.78, 88.68) * mm});
            skLineSegment(sketch, "E831", {"start": v(410.78, 88.68) * mm, "end": v(380.43, 101.26) * mm});
            skLineSegment(sketch, "E832", {"start": v(380.43, 101.26) * mm, "end": v(373.14, 83.66) * mm});
            skLineSegment(sketch, "E833", {"start": v(403.5, 71.08) * mm, "end": v(373.14, 83.66) * mm});
            skLineSegment(sketch, "E834", {"start": v(320.77, 105.36) * mm, "end": v(328.07, 122.96) * mm});
            skLineSegment(sketch, "E835", {"start": v(328.07, 122.96) * mm, "end": v(293.25, 137.4) * mm});
            skLineSegment(sketch, "E836", {"start": v(293.25, 137.4) * mm, "end": v(285.95, 119.8) * mm});
            skLineSegment(sketch, "E837", {"start": v(320.77, 105.36) * mm, "end": v(285.95, 119.8) * mm});
            skLineSegment(sketch, "E838", {"start": v(185.79, 83.83) * mm, "end": v(178.5, 101.43) * mm});
            skLineSegment(sketch, "E839", {"start": v(178.5, 101.43) * mm, "end": v(148.14, 88.86) * mm});
            skLineSegment(sketch, "E840", {"start": v(155.43, 71.25) * mm, "end": v(148.14, 88.86) * mm});
            skLineSegment(sketch, "E841", {"start": v(230.86, 123.12) * mm, "end": v(238.15, 105.52) * mm});
            skLineSegment(sketch, "E842", {"start": v(238.15, 105.52) * mm, "end": v(272.97, 119.94) * mm});
            skLineSegment(sketch, "E843", {"start": v(272.97, 119.94) * mm, "end": v(265.68, 137.54) * mm});
            skLineSegment(sketch, "E844", {"start": v(230.86, 123.12) * mm, "end": v(265.68, 137.54) * mm});
            skLineSegment(sketch, "E845", {"start": v(83.71, 185.51) * mm, "end": v(71.14, 155.15) * mm});
            skLineSegment(sketch, "E846", {"start": v(71.14, 155.15) * mm, "end": v(88.74, 147.86) * mm});
            skLineSegment(sketch, "E847", {"start": v(88.74, 147.86) * mm, "end": v(101.31, 178.22) * mm});
            skLineSegment(sketch, "E848", {"start": v(83.71, 185.51) * mm, "end": v(101.31, 178.22) * mm});
            skLineSegment(sketch, "E849", {"start": v(105.4, 237.88) * mm, "end": v(123, 230.59) * mm});
            skLineSegment(sketch, "E850", {"start": v(123, 230.59) * mm, "end": v(137.43, 265.4) * mm});
            skLineSegment(sketch, "E851", {"start": v(137.43, 265.4) * mm, "end": v(119.83, 272.7) * mm});
            skLineSegment(sketch, "E852", {"start": v(105.4, 237.88) * mm, "end": v(119.83, 272.7) * mm});
            skLineSegment(sketch, "E853", {"start": v(28.1, 1089.5) * mm, "end": v(14.12, 1103.47) * mm});
            skLineSegment(sketch, "E854", {"start": v(22.51, 1111.86) * mm, "end": v(5.75, 1095.1) * mm});
            skLineSegment(sketch, "E855", {"start": v(530.95, 1089.52) * mm, "end": v(544.92, 1103.48) * mm});
            skLineSegment(sketch, "E856", {"start": v(544.92, 1103.48) * mm, "end": v(558.88, 1089.51) * mm});
            skLineSegment(sketch, "E857", {"start": v(553.3, 1095.1) * mm, "end": v(536.54, 1111.87) * mm});
            skLineSegment(sketch, "E858", {"start": v(530.86, 27.93) * mm, "end": v(544.83, 13.97) * mm});
            skLineSegment(sketch, "E859", {"start": v(544.83, 13.97) * mm, "end": v(536.47, 5.6) * mm});
            skLineSegment(sketch, "E860", {"start": v(530.88, 0.02) * mm, "end": v(553.22, 22.36) * mm});
            skLineSegment(sketch, "E861", {"start": v(28.68, 28.44) * mm, "end": v(14.72, 14.47) * mm});
            skLineSegment(sketch, "E862", {"start": v(14.72, 14.47) * mm, "end": v(6.32, 22.85) * mm});
            skLineSegment(sketch, "E863", {"start": v(0.73, 28.44) * mm, "end": v(23.16, 6.03) * mm});
            skPoint(sketch, "E864", {"position": v(279.8, 0.24) * mm});
            skPoint(sketch, "E865", {"position": v(558.84, 558.72) * mm});
            skPoint(sketch, "E866", {"position": v(279.8, 1117.44) * mm});
            skPoint(sketch, "E867", {"position": v(0.46, 558.72) * mm});
            skLineSegment(sketch, "E868", {"start": v(0.46, 558.72) * mm, "end": v(558.84, 558.72) * mm, "construction": true});
            skLineSegment(sketch, "E869", {"start": v(279.8, 38.35) * mm, "end": v(279.8, 1117.44) * mm, "construction": true});
            skLineSegment(sketch, "E870", {"start": v(279.8, 0.24) * mm, "end": v(279.8, 38.35) * mm});
            skLineSegment(sketch, "E871", {"start": v(0.46, 558.72) * mm, "end": v(76.7, 558.72) * mm});
            skLineSegment(sketch, "E872", {"start": v(558.84, 558.72) * mm, "end": v(482.6, 558.72) * mm});
            skLineSegment(sketch, "E873", {"start": v(279.8, 1117.44) * mm, "end": v(279.8, 1079.3) * mm, "construction": true});
            skLineSegment(sketch, "E874", {"start": v(36.6, 0.46) * mm, "end": v(117.1, 0.39) * mm});
            skLineSegment(sketch, "E875", {"start": v(0.74, 36.32) * mm, "end": v(0.62, 250.4) * mm});
            skLineSegment(sketch, "E876", {"start": v(482.6, 558.72) * mm, "end": v(482.6, 433.07) * mm});
            skLineSegment(sketch, "E877", {"start": v(482.6, 558.72) * mm, "end": v(482.6, 685.72) * mm});
            skLineSegment(sketch, "E878", {"start": v(76.7, 558.72) * mm, "end": v(76.7, 431.72) * mm});
            skLineSegment(sketch, "E879", {"start": v(76.7, 558.72) * mm, "end": v(76.7, 685.72) * mm});
            skLineSegment(sketch, "E880.0", {"start": v(32.08, 791.06) * mm, "end": v(76.7, 683.23) * mm});
            skLineSegment(sketch, "E881.0", {"start": v(32.33, 326.95) * mm, "end": v(76.7, 434.06) * mm});
            skLineSegment(sketch, "E882.0", {"start": v(527.11, 791.9) * mm, "end": v(482.6, 684.47) * mm});
            skLineSegment(sketch, "E883.0", {"start": v(527.07, 325.68) * mm, "end": v(482.6, 433.07) * mm});
            skLineSegment(sketch, "E884.trimOffspring", {"start": v(558.82, 249.03) * mm, "end": v(558.8, 35.83) * mm});
            skLineSegment(sketch, "E885.trimOffspring", {"start": v(0.29, 867.9) * mm, "end": v(0.18, 1081.62) * mm});
            skLineSegment(sketch, "E886.trimOffspring", {"start": v(442.66, 1117.45) * mm, "end": v(523.06, 1117.45) * mm});
            skLineSegment(sketch, "E887", {"start": v(185.79, 83.83) * mm, "end": v(155.43, 71.25) * mm});
            skLineSegment(sketch, "E888.trimOffspring", {"start": v(442.08, 0.1) * mm, "end": v(522.98, 0.03) * mm});
            skLineSegment(sketch, "E889.trimOffspring", {"start": v(128.2, 558.72) * mm, "end": v(144.35, 519.71) * mm});
            skLineSegment(sketch, "E890.trimOffspring", {"start": v(128.27, 558.58) * mm, "end": v(144.36, 597.43) * mm});
            skLineSegment(sketch, "E891.trimOffspring", {"start": v(430.55, 558.72) * mm, "end": v(414.4, 597.69) * mm});
            skLineSegment(sketch, "E892.trimOffspring", {"start": v(430.52, 558.8) * mm, "end": v(414.4, 519.92) * mm});
            skLineSegment(sketch, "E893.trimOffspring", {"start": v(238.16, 558.72) * mm, "end": v(238.23, 558.55) * mm});
            skLineSegment(sketch, "E894.trimOffspring", {"start": v(320.58, 558.72) * mm, "end": v(320.54, 558.81) * mm});
            skArc(sketch, "E895.filletArc", {"start": v(0.74, 36.32) * mm, "mid": v(2.19, 29.03) * mm, "end": v(6.32, 22.85) * mm});
            skPoint(sketch, "E896.visualSharp", {"position": v(28.73, 0.47) * mm});
            skArc(sketch, "E896.filletArc", {"start": v(23.16, 6.03) * mm, "mid": v(29.33, 1.91) * mm, "end": v(36.6, 0.46) * mm});
            skPoint(sketch, "E897.visualSharp", {"position": v(530.88, 0.02) * mm});
            skArc(sketch, "E897.filletArc", {"start": v(522.98, 0.03) * mm, "mid": v(530.28, 1.48) * mm, "end": v(536.47, 5.6) * mm});
            skPoint(sketch, "E898.visualSharp", {"position": v(558.8, 27.94) * mm});
            skArc(sketch, "E898.filletArc", {"start": v(553.22, 22.36) * mm, "mid": v(557.35, 28.54) * mm, "end": v(558.8, 35.83) * mm});
            skPoint(sketch, "E899.visualSharp", {"position": v(28.1, 1117.44) * mm});
            skArc(sketch, "E899.filletArc", {"start": v(35.98, 1117.44) * mm, "mid": v(28.7, 1115.99) * mm, "end": v(22.51, 1111.86) * mm});
            skPoint(sketch, "E900.newPointA", {"position": v(0.16, 1089.5) * mm});
            skArc(sketch, "E900.filletArc", {"start": v(5.75, 1095.1) * mm, "mid": v(1.62, 1088.91) * mm, "end": v(0.18, 1081.62) * mm});
            skPoint(sketch, "E901.visualSharp", {"position": v(530.96, 1117.45) * mm});
            skArc(sketch, "E901.filletArc", {"start": v(536.54, 1111.87) * mm, "mid": v(530.35, 1116) * mm, "end": v(523.06, 1117.45) * mm});
            skPoint(sketch, "E902.visualSharp", {"position": v(558.88, 1089.51) * mm});
            skArc(sketch, "E902.filletArc", {"start": v(558.88, 1081.62) * mm, "mid": v(557.43, 1088.91) * mm, "end": v(553.3, 1095.1) * mm});
            skLineSegment(sketch, "E903", {"start": v(558.82, 249.03) * mm, "end": v(558.87, 868.54) * mm});
            skLineSegment(sketch, "E904.0", {"start": v(527.07, 249.04) * mm, "end": v(527.12, 868.54) * mm});
            skLineSegment(sketch, "E905", {"start": v(117.1, 0.39) * mm, "end": v(442.08, 0.1) * mm});
            skLineSegment(sketch, "E906.0", {"start": v(203.69, 63.75) * mm, "end": v(107.37, 23.86) * mm});
            skLineSegment(sketch, "E906.1", {"start": v(279.8, 63.75) * mm, "end": v(203.69, 63.75) * mm});
            skLineSegment(sketch, "E906.2", {"start": v(279.8, 63.75) * mm, "end": v(354.83, 63.75) * mm});
            skLineSegment(sketch, "E906.3", {"start": v(451.8, 23.57) * mm, "end": v(354.83, 63.75) * mm});
            skLineSegment(sketch, "E907.0", {"start": v(117.12, 32.14) * mm, "end": v(442.1, 31.85) * mm});
            skLineSegment(sketch, "E908", {"start": v(116.54, 1117.44) * mm, "end": v(442.66, 1117.45) * mm});
            skLineSegment(sketch, "E909.0", {"start": v(203.72, 1053.9) * mm, "end": v(106.83, 1093.97) * mm});
            skLineSegment(sketch, "E909.1", {"start": v(279.8, 1053.9) * mm, "end": v(203.72, 1053.9) * mm});
            skLineSegment(sketch, "E909.2", {"start": v(279.8, 1053.9) * mm, "end": v(355.6, 1053.9) * mm});
            skLineSegment(sketch, "E909.3", {"start": v(452.37, 1093.98) * mm, "end": v(355.6, 1053.9) * mm});
            skLineSegment(sketch, "E910.0", {"start": v(116.54, 1085.69) * mm, "end": v(442.66, 1085.7) * mm});
            skLineSegment(sketch, "E911", {"start": v(0.62, 250.4) * mm, "end": v(0.29, 867.9) * mm});
            skLineSegment(sketch, "E912.0", {"start": v(32.37, 250.42) * mm, "end": v(32.04, 867.92) * mm});
            skSolve(sketch);
        }
        {
            var Q0;
            Q0 = qSketchRegion(id + "F57", true);
            extrude(context, id + "F58", {"entities" : qUnion([Q0]), "depth" : 19.05 * mm});
        }
    });
